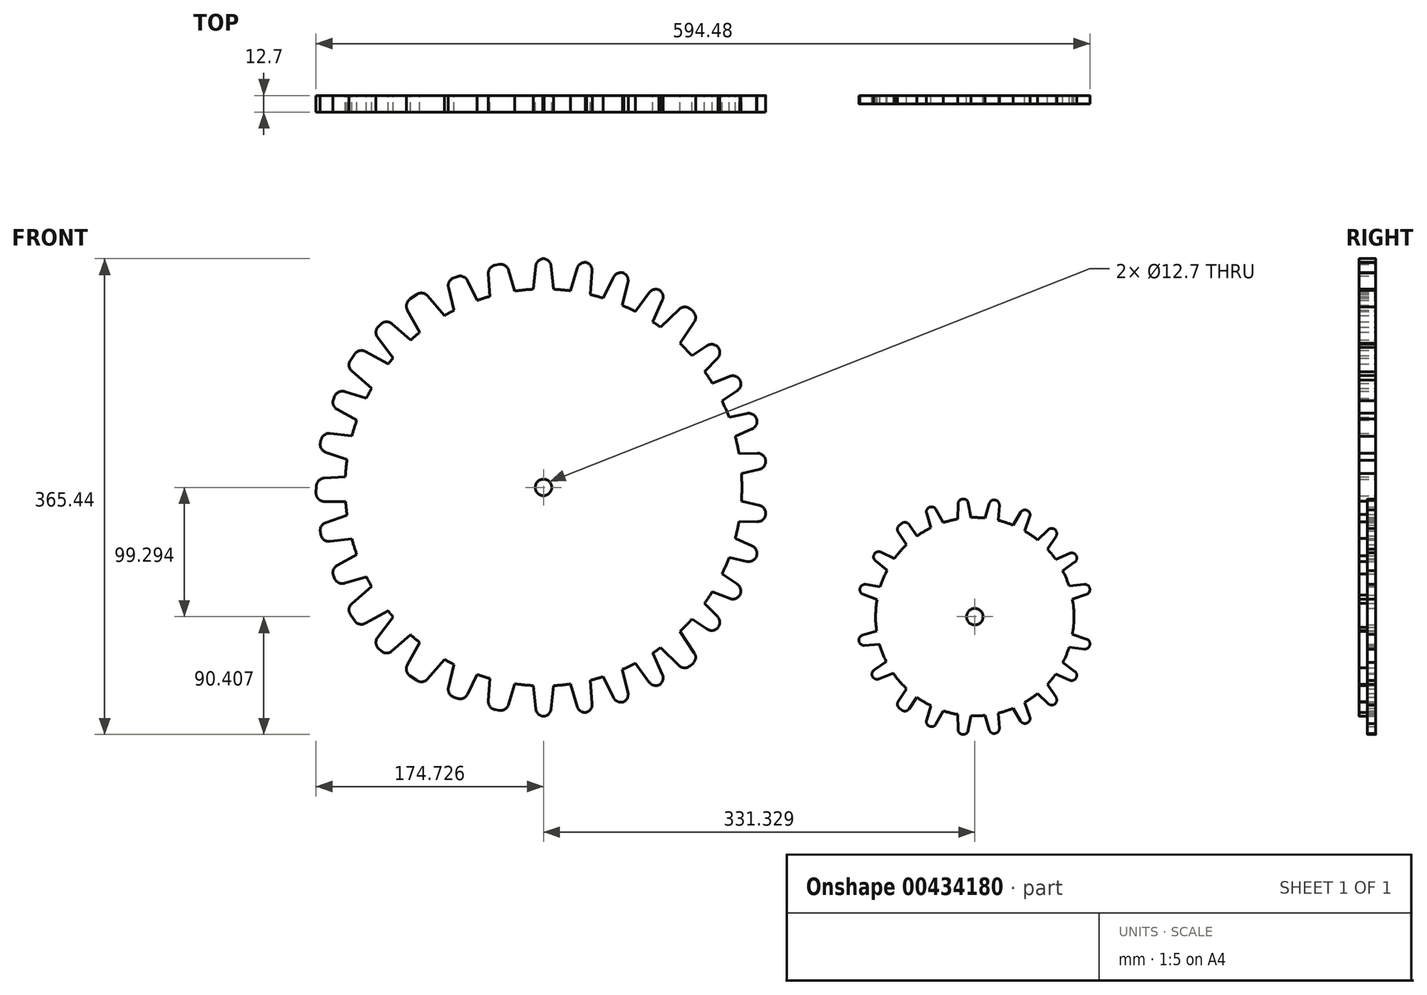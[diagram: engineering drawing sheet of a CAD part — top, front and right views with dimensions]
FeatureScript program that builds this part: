
annotation { "Feature Type Name" : "Feature", "Feature Type Description" : "" }
export const myFeature = defineFeature(function(context is Context, id is Id, definition is map)
    precondition{}
    {
        {
            var Q0;
            Q0=qCreatedBy(makeId("Front.planeOp"),FACE);
            var sketch = newSketch(context, id + "F0", { "sketchPlane" : qUnion([Q0])});
            skCircle(sketch, "E0", {"center": v(-40.91, 6.31) * mm, "radius": 152.4 * mm});
            skCircle(sketch, "E1", {"center": v(290.41, -92.98) * mm, "radius": 76.2 * mm});
            skCircle(sketch, "E2", {"center": v(-40.91, 6.31) * mm, "radius": 6.35 * mm});
            skCircle(sketch, "E3", {"center": v(290.41, -92.98) * mm, "radius": 6.35 * mm});
            skLineSegment(sketch, "E4", {"start": v(214.21, -92.98) * mm, "end": v(366.61, -92.98) * mm, "construction": true});
            skLineSegment(sketch, "E5.bottom", {"start": v(281, -2.62) * mm, "end": v(281.28, -2.6) * mm});
            skLineSegment(sketch, "E5.top", {"start": v(277.33, -17.92) * mm, "end": v(287.54, -16.84) * mm});
            skLineSegment(sketch, "E5.left", {"start": v(277.53, -6.35) * mm, "end": v(277.33, -17.92) * mm});
            skLineSegment(sketch, "E5.right", {"start": v(285.35, -5.65) * mm, "end": v(287.54, -16.84) * mm});
            skPoint(sketch, "E6.visualSharp", {"position": v(277.59, -2.92) * mm});
            skArc(sketch, "E6.filletArc", {"start": v(278, -2.88) * mm, "mid": v(277.7, -3.02) * mm, "end": v(277.58, -3.32) * mm});
            skPoint(sketch, "E7.visualSharp", {"position": v(284.69, -2.3) * mm});
            skArc(sketch, "E7.filletArc", {"start": v(284.77, -2.7) * mm, "mid": v(284.6, -2.42) * mm, "end": v(284.28, -2.33) * mm});
            skLineSegment(sketch, "E8.bottom", {"start": v(305.87, -3.37) * mm, "end": v(306.13, -3.42) * mm});
            skLineSegment(sketch, "E8.top", {"start": v(298.35, -17.2) * mm, "end": v(308.47, -18.95) * mm});
            skLineSegment(sketch, "E8.left", {"start": v(301.54, -6.07) * mm, "end": v(298.35, -17.2) * mm});
            skLineSegment(sketch, "E8.right", {"start": v(309.27, -7.44) * mm, "end": v(308.47, -18.95) * mm});
            skPoint(sketch, "E9.visualSharp", {"position": v(302.49, -2.78) * mm});
            skArc(sketch, "E9.filletArc", {"start": v(302.89, -2.85) * mm, "mid": v(302.57, -2.9) * mm, "end": v(302.38, -3.17) * mm});
            skPoint(sketch, "E10.visualSharp", {"position": v(309.5, -4.01) * mm});
            skArc(sketch, "E10.filletArc", {"start": v(309.48, -4.42) * mm, "mid": v(309.38, -4.11) * mm, "end": v(309.1, -3.94) * mm});
            skLineSegment(sketch, "E11.bottom", {"start": v(330.62, -11.41) * mm, "end": v(330.84, -11.52) * mm});
            skLineSegment(sketch, "E11.top", {"start": v(319.73, -22.65) * mm, "end": v(328.9, -27.21) * mm});
            skLineSegment(sketch, "E11.left", {"start": v(325.62, -12.84) * mm, "end": v(319.73, -22.65) * mm});
            skLineSegment(sketch, "E11.right", {"start": v(332.7, -16.15) * mm, "end": v(328.9, -27.21) * mm});
            skPoint(sketch, "E12.visualSharp", {"position": v(327.45, -9.79) * mm});
            skArc(sketch, "E12.filletArc", {"start": v(327.83, -9.98) * mm, "mid": v(327.5, -9.95) * mm, "end": v(327.23, -10.15) * mm});
            skPoint(sketch, "E13.visualSharp", {"position": v(333.78, -13.03) * mm});
            skArc(sketch, "E13.filletArc", {"start": v(333.65, -13.4) * mm, "mid": v(333.64, -13.08) * mm, "end": v(333.43, -12.85) * mm});
            skLineSegment(sketch, "E14.bottom", {"start": v(255.53, -8.97) * mm, "end": v(255.78, -8.87) * mm});
            skLineSegment(sketch, "E14.top", {"start": v(256.67, -24.66) * mm, "end": v(266.15, -20.75) * mm});
            skLineSegment(sketch, "E14.left", {"start": v(253.35, -13.58) * mm, "end": v(256.67, -24.66) * mm});
            skLineSegment(sketch, "E14.right", {"start": v(260.6, -10.56) * mm, "end": v(266.15, -20.75) * mm});
            skPoint(sketch, "E15.visualSharp", {"position": v(252.37, -10.3) * mm});
            skArc(sketch, "E15.filletArc", {"start": v(252.74, -10.13) * mm, "mid": v(252.5, -10.36) * mm, "end": v(252.48, -10.68) * mm});
            skPoint(sketch, "E16.visualSharp", {"position": v(258.95, -7.55) * mm});
            skArc(sketch, "E16.filletArc", {"start": v(259.14, -7.9) * mm, "mid": v(258.9, -7.7) * mm, "end": v(258.57, -7.7) * mm});
            skLineSegment(sketch, "E17.bottom", {"start": v(232.31, -22.96) * mm, "end": v(234.21, -21.37) * mm});
            skLineSegment(sketch, "E17.top", {"start": v(238.08, -37.6) * mm, "end": v(245.99, -31.07) * mm});
            skLineSegment(sketch, "E17.left", {"start": v(231.6, -28) * mm, "end": v(238.08, -37.6) * mm});
            skLineSegment(sketch, "E17.right", {"start": v(239.8, -22.12) * mm, "end": v(245.99, -31.07) * mm});
            skPoint(sketch, "E18.visualSharp", {"position": v(229.69, -25.16) * mm});
            skArc(sketch, "E18.filletArc", {"start": v(230, -24.9) * mm, "mid": v(229.84, -25.19) * mm, "end": v(229.92, -25.5) * mm});
            skPoint(sketch, "E19.visualSharp", {"position": v(237.42, -18.68) * mm});
            skArc(sketch, "E19.filletArc", {"start": v(237.64, -19.02) * mm, "mid": v(237.34, -18.9) * mm, "end": v(237.03, -19) * mm});
            skLineSegment(sketch, "E20.bottom", {"start": v(213.25, -44.93) * mm, "end": v(213.4, -44.7) * mm});
            skLineSegment(sketch, "E20.top", {"start": v(223.17, -57.14) * mm, "end": v(228.6, -48.42) * mm});
            skLineSegment(sketch, "E20.left", {"start": v(214.1, -49.95) * mm, "end": v(223.17, -57.14) * mm});
            skLineSegment(sketch, "E20.right", {"start": v(218.3, -43.33) * mm, "end": v(228.6, -48.42) * mm});
            skPoint(sketch, "E21.visualSharp", {"position": v(211.41, -47.82) * mm});
            skArc(sketch, "E21.filletArc", {"start": v(211.63, -47.48) * mm, "mid": v(211.57, -47.8) * mm, "end": v(211.73, -48.08) * mm});
            skPoint(sketch, "E22.visualSharp", {"position": v(215.23, -41.8) * mm});
            skArc(sketch, "E22.filletArc", {"start": v(215.6, -41.99) * mm, "mid": v(215.27, -41.96) * mm, "end": v(215.01, -42.15) * mm});
            skLineSegment(sketch, "E23.bottom", {"start": v(202.22, -71.24) * mm, "end": v(202.3, -70.97) * mm});
            skLineSegment(sketch, "E23.top", {"start": v(215.34, -79.93) * mm, "end": v(217.78, -69.95) * mm});
            skLineSegment(sketch, "E23.left", {"start": v(204.54, -75.78) * mm, "end": v(215.34, -79.93) * mm});
            skLineSegment(sketch, "E23.right", {"start": v(206.56, -68.2) * mm, "end": v(217.78, -69.95) * mm});
            skPoint(sketch, "E24.visualSharp", {"position": v(201.34, -74.55) * mm});
            skArc(sketch, "E24.filletArc", {"start": v(201.44, -74.16) * mm, "mid": v(201.48, -74.48) * mm, "end": v(201.72, -74.7) * mm});
            skPoint(sketch, "E25.visualSharp", {"position": v(203.18, -67.67) * mm});
            skArc(sketch, "E25.filletArc", {"start": v(203.58, -67.73) * mm, "mid": v(203.27, -67.8) * mm, "end": v(203.08, -68.06) * mm});
            skLineSegment(sketch, "E26.bottom", {"start": v(352.11, -26.2) * mm, "end": v(352.26, -26.34) * mm});
            skLineSegment(sketch, "E26.top", {"start": v(338.67, -34.01) * mm, "end": v(346.12, -41) * mm});
            skLineSegment(sketch, "E26.left", {"start": v(346.8, -26.17) * mm, "end": v(338.67, -34.01) * mm});
            skLineSegment(sketch, "E26.right", {"start": v(352.74, -31.18) * mm, "end": v(346.12, -41) * mm});
            skPoint(sketch, "E27.visualSharp", {"position": v(349.46, -23.6) * mm});
            skArc(sketch, "E27.filletArc", {"start": v(349.78, -23.9) * mm, "mid": v(349.46, -23.77) * mm, "end": v(349.15, -23.9) * mm});
            skPoint(sketch, "E28.visualSharp", {"position": v(354.51, -28.56) * mm});
            skArc(sketch, "E28.filletArc", {"start": v(354.3, -28.87) * mm, "mid": v(354.38, -28.57) * mm, "end": v(354.25, -28.3) * mm});
            skLineSegment(sketch, "E29.bottom", {"start": v(368.1, -45.7) * mm, "end": v(368.24, -45.94) * mm});
            skLineSegment(sketch, "E29.top", {"start": v(352.64, -49) * mm, "end": v(358, -57.77) * mm});
            skLineSegment(sketch, "E29.left", {"start": v(363.32, -44.24) * mm, "end": v(352.64, -49) * mm});
            skLineSegment(sketch, "E29.right", {"start": v(367.25, -51.04) * mm, "end": v(358, -57.77) * mm});
            skPoint(sketch, "E30.visualSharp", {"position": v(366.34, -42.9) * mm});
            skArc(sketch, "E30.filletArc", {"start": v(366.55, -43.23) * mm, "mid": v(366.3, -43.04) * mm, "end": v(365.98, -43.06) * mm});
            skPoint(sketch, "E31.visualSharp", {"position": v(370.13, -48.95) * mm});
            skArc(sketch, "E31.filletArc", {"start": v(369.79, -49.2) * mm, "mid": v(369.96, -48.92) * mm, "end": v(369.9, -48.6) * mm});
            skLineSegment(sketch, "E32.bottom", {"start": v(378.65, -70.95) * mm, "end": v(378.72, -71.22) * mm});
            skLineSegment(sketch, "E32.top", {"start": v(362.91, -69.52) * mm, "end": v(365.4, -79.49) * mm});
            skLineSegment(sketch, "E32.left", {"start": v(374.5, -68.13) * mm, "end": v(362.91, -69.52) * mm});
            skLineSegment(sketch, "E32.right", {"start": v(376.26, -75.79) * mm, "end": v(365.4, -79.49) * mm});
            skPoint(sketch, "E33.visualSharp", {"position": v(377.8, -67.74) * mm});
            skArc(sketch, "E33.filletArc", {"start": v(377.9, -68.12) * mm, "mid": v(377.72, -67.86) * mm, "end": v(377.41, -67.78) * mm});
            skPoint(sketch, "E34.visualSharp", {"position": v(379.6, -74.65) * mm});
            skArc(sketch, "E34.filletArc", {"start": v(379.21, -74.78) * mm, "mid": v(379.46, -74.57) * mm, "end": v(379.5, -74.24) * mm});
            skArc(sketch, "E35.MirrorCS", {"start": v(259.14, -178.06) * mm, "mid": v(258.9, -178.27) * mm, "end": v(258.57, -178.26) * mm});
            skArc(sketch, "E36.MirrorCS", {"start": v(278, -183.08) * mm, "mid": v(277.7, -182.94) * mm, "end": v(277.58, -182.64) * mm});
            skArc(sketch, "E37.MirrorCS", {"start": v(366.55, -142.74) * mm, "mid": v(366.3, -142.93) * mm, "end": v(365.98, -142.91) * mm});
            skArc(sketch, "E38.MirrorCS", {"start": v(309.48, -181.54) * mm, "mid": v(309.38, -181.85) * mm, "end": v(309.1, -182.02) * mm});
            skLineSegment(sketch, "E39.MirrorCS", {"start": v(352.11, -159.77) * mm, "end": v(352.26, -159.63) * mm});
            skArc(sketch, "E40.MirrorCS", {"start": v(349.78, -162.06) * mm, "mid": v(349.46, -162.2) * mm, "end": v(349.15, -162.07) * mm});
            skArc(sketch, "E41.MirrorCS", {"start": v(377.9, -117.85) * mm, "mid": v(377.72, -118.1) * mm, "end": v(377.41, -118.18) * mm});
            skArc(sketch, "E42.MirrorCS", {"start": v(327.83, -175.99) * mm, "mid": v(327.5, -176.02) * mm, "end": v(327.23, -175.82) * mm});
            skArc(sketch, "E43.MirrorCS", {"start": v(354.3, -157.1) * mm, "mid": v(354.38, -157.4) * mm, "end": v(354.25, -157.67) * mm});
            skLineSegment(sketch, "E44.MirrorCS", {"start": v(368.1, -140.26) * mm, "end": v(368.24, -140.03) * mm});
            skLineSegment(sketch, "E45.MirrorCS", {"start": v(281, -183.35) * mm, "end": v(281.28, -183.37) * mm});
            skArc(sketch, "E46.MirrorCS", {"start": v(252.74, -175.83) * mm, "mid": v(252.5, -175.6) * mm, "end": v(252.48, -175.28) * mm});
            skArc(sketch, "E47.MirrorCS", {"start": v(284.77, -183.27) * mm, "mid": v(284.6, -183.55) * mm, "end": v(284.28, -183.64) * mm});
            skLineSegment(sketch, "E48.MirrorCS", {"start": v(330.62, -174.56) * mm, "end": v(330.84, -174.44) * mm});
            skArc(sketch, "E49.MirrorCS", {"start": v(237.64, -166.94) * mm, "mid": v(237.34, -167.07) * mm, "end": v(237.03, -166.97) * mm});
            skArc(sketch, "E50.MirrorCS", {"start": v(369.79, -136.76) * mm, "mid": v(369.96, -137.04) * mm, "end": v(369.9, -137.37) * mm});
            skLineSegment(sketch, "E51.MirrorCS", {"start": v(255.53, -177) * mm, "end": v(255.78, -177.1) * mm});
            skArc(sketch, "E52.MirrorCS", {"start": v(333.65, -172.57) * mm, "mid": v(333.64, -172.88) * mm, "end": v(333.43, -173.12) * mm});
            skLineSegment(sketch, "E53.MirrorCS", {"start": v(232.31, -163) * mm, "end": v(234.21, -164.6) * mm});
            skArc(sketch, "E54.MirrorCS", {"start": v(230, -161.06) * mm, "mid": v(229.84, -160.78) * mm, "end": v(229.92, -160.46) * mm});
            skLineSegment(sketch, "E55.MirrorCS", {"start": v(305.87, -182.6) * mm, "end": v(306.13, -182.55) * mm});
            skArc(sketch, "E56.MirrorCS", {"start": v(302.89, -183.12) * mm, "mid": v(302.57, -183.06) * mm, "end": v(302.38, -182.8) * mm});
            skLineSegment(sketch, "E57.MirrorCS", {"start": v(378.65, -115.01) * mm, "end": v(378.72, -114.74) * mm});
            skArc(sketch, "E58.MirrorCS", {"start": v(379.21, -111.18) * mm, "mid": v(379.46, -111.4) * mm, "end": v(379.5, -111.73) * mm});
            skPoint(sketch, "E59.MirrorP", {"position": v(354.51, -157.4) * mm});
            skPoint(sketch, "E60.MirrorP", {"position": v(258.95, -178.42) * mm});
            skLineSegment(sketch, "E61.MirrorCS", {"start": v(285.35, -180.31) * mm, "end": v(287.54, -169.13) * mm});
            skPoint(sketch, "E62.MirrorP", {"position": v(277.59, -183.05) * mm});
            skPoint(sketch, "E63.MirrorP", {"position": v(379.6, -111.32) * mm});
            skPoint(sketch, "E64.MirrorP", {"position": v(237.42, -167.29) * mm});
            skLineSegment(sketch, "E65.MirrorCS", {"start": v(332.7, -169.81) * mm, "end": v(328.9, -158.75) * mm});
            skLineSegment(sketch, "E66.MirrorCS", {"start": v(231.6, -157.96) * mm, "end": v(238.08, -148.36) * mm});
            skPoint(sketch, "E67.MirrorP", {"position": v(229.69, -160.8) * mm});
            skLineSegment(sketch, "E68.MirrorCS", {"start": v(256.67, -161.3) * mm, "end": v(266.15, -165.22) * mm});
            skLineSegment(sketch, "E69.MirrorCS", {"start": v(260.6, -175.4) * mm, "end": v(266.15, -165.22) * mm});
            skLineSegment(sketch, "E70.MirrorCS", {"start": v(325.62, -173.13) * mm, "end": v(319.73, -163.32) * mm});
            skLineSegment(sketch, "E71.MirrorCS", {"start": v(374.5, -117.83) * mm, "end": v(362.91, -116.45) * mm});
            skPoint(sketch, "E72.MirrorP", {"position": v(327.45, -176.18) * mm});
            skLineSegment(sketch, "E73.MirrorCS", {"start": v(298.35, -168.77) * mm, "end": v(308.47, -167.01) * mm});
            skLineSegment(sketch, "E74.MirrorCS", {"start": v(362.91, -116.45) * mm, "end": v(365.4, -106.48) * mm});
            skPoint(sketch, "E75.MirrorP", {"position": v(366.34, -143.07) * mm});
            skPoint(sketch, "E76.MirrorP", {"position": v(370.13, -137.01) * mm});
            skLineSegment(sketch, "E77.MirrorCS", {"start": v(367.25, -134.92) * mm, "end": v(358, -128.2) * mm});
            skPoint(sketch, "E78.MirrorP", {"position": v(349.46, -162.37) * mm});
            skPoint(sketch, "E79.MirrorP", {"position": v(252.37, -175.67) * mm});
            skPoint(sketch, "E80.MirrorP", {"position": v(284.69, -183.67) * mm});
            skLineSegment(sketch, "E81.MirrorCS", {"start": v(301.54, -179.9) * mm, "end": v(298.35, -168.77) * mm});
            skLineSegment(sketch, "E82.MirrorCS", {"start": v(352.74, -154.78) * mm, "end": v(346.12, -144.97) * mm});
            skLineSegment(sketch, "E83.MirrorCS", {"start": v(376.26, -110.18) * mm, "end": v(365.4, -106.48) * mm});
            skLineSegment(sketch, "E84.MirrorCS", {"start": v(238.08, -148.36) * mm, "end": v(245.99, -154.9) * mm});
            skLineSegment(sketch, "E85.MirrorCS", {"start": v(346.8, -159.8) * mm, "end": v(338.67, -151.95) * mm});
            skLineSegment(sketch, "E86.MirrorCS", {"start": v(309.27, -178.53) * mm, "end": v(308.47, -167.01) * mm});
            skPoint(sketch, "E87.MirrorP", {"position": v(309.5, -181.95) * mm});
            skLineSegment(sketch, "E88.MirrorCS", {"start": v(319.73, -163.32) * mm, "end": v(328.9, -158.75) * mm});
            skLineSegment(sketch, "E89.MirrorCS", {"start": v(253.35, -172.39) * mm, "end": v(256.67, -161.3) * mm});
            skLineSegment(sketch, "E90.MirrorCS", {"start": v(277.53, -179.62) * mm, "end": v(277.33, -168.05) * mm});
            skPoint(sketch, "E91.MirrorP", {"position": v(333.78, -172.94) * mm});
            skLineSegment(sketch, "E92.MirrorCS", {"start": v(338.67, -151.95) * mm, "end": v(346.12, -144.97) * mm});
            skPoint(sketch, "E93.MirrorP", {"position": v(302.49, -183.19) * mm});
            skPoint(sketch, "E94.MirrorP", {"position": v(377.8, -118.23) * mm});
            skLineSegment(sketch, "E95.MirrorCS", {"start": v(239.8, -163.85) * mm, "end": v(245.99, -154.9) * mm});
            skLineSegment(sketch, "E96.MirrorCS", {"start": v(363.32, -141.72) * mm, "end": v(352.64, -136.97) * mm});
            skLineSegment(sketch, "E97.MirrorCS", {"start": v(277.33, -168.05) * mm, "end": v(287.54, -169.13) * mm});
            skLineSegment(sketch, "E98.MirrorCS", {"start": v(352.64, -136.97) * mm, "end": v(358, -128.2) * mm});
            skLineSegment(sketch, "E99", {"start": v(-193.31, 6.31) * mm, "end": v(111.49, 6.31) * mm, "construction": true});
            skLineSegment(sketch, "E100.bottom", {"start": v(-215.94, -4) * mm, "end": v(-215.1, 12.77) * mm});
            skLineSegment(sketch, "E100.top", {"start": v(-192.93, -4.45) * mm, "end": v(-193.1, 14.48) * mm});
            skLineSegment(sketch, "E100.left", {"start": v(-209.28, -4.48) * mm, "end": v(-192.93, -4.45) * mm});
            skLineSegment(sketch, "E100.right", {"start": v(-209.4, 13.51) * mm, "end": v(-193.1, 14.48) * mm});
            skPoint(sketch, "E101.visualSharp", {"position": v(-215.96, -4.49) * mm});
            skArc(sketch, "E101.filletArc", {"start": v(-215.94, -4) * mm, "mid": v(-215.81, -4.35) * mm, "end": v(-215.48, -4.49) * mm});
            skPoint(sketch, "E102.visualSharp", {"position": v(-215.09, 13.18) * mm});
            skArc(sketch, "E102.filletArc", {"start": v(-214.68, 13.2) * mm, "mid": v(-214.98, 13.07) * mm, "end": v(-215.1, 12.77) * mm});
            skLineSegment(sketch, "E103.bottom", {"start": v(-212.29, 40.71) * mm, "end": v(-211.8, 42.9) * mm});
            skLineSegment(sketch, "E103.top", {"start": v(-191.8, 27.73) * mm, "end": v(-188.1, 45.82) * mm});
            skLineSegment(sketch, "E103.left", {"start": v(-208.14, 33.3) * mm, "end": v(-191.8, 27.73) * mm});
            skLineSegment(sketch, "E103.right", {"start": v(-204.86, 47.8) * mm, "end": v(-188.1, 45.82) * mm});
            skPoint(sketch, "E104.visualSharp", {"position": v(-213.55, 35.14) * mm});
            skArc(sketch, "E104.filletArc", {"start": v(-213.46, 35.53) * mm, "mid": v(-213.42, 35.21) * mm, "end": v(-213.17, 35) * mm});
            skPoint(sketch, "E105.visualSharp", {"position": v(-210.53, 48.46) * mm});
            skArc(sketch, "E105.filletArc", {"start": v(-210.12, 48.41) * mm, "mid": v(-210.44, 48.33) * mm, "end": v(-210.62, 48.06) * mm});
            skLineSegment(sketch, "E106.bottom", {"start": v(-202.2, 74.2) * mm, "end": v(-201.34, 76.26) * mm});
            skLineSegment(sketch, "E106.top", {"start": v(-184.28, 58) * mm, "end": v(-177, 74.91) * mm});
            skLineSegment(sketch, "E106.left", {"start": v(-199.36, 66.2) * mm, "end": v(-184.28, 58) * mm});
            skLineSegment(sketch, "E106.right", {"start": v(-193.65, 79.9) * mm, "end": v(-177, 74.91) * mm});
            skPoint(sketch, "E107.visualSharp", {"position": v(-204.38, 68.92) * mm});
            skArc(sketch, "E107.filletArc", {"start": v(-204.23, 69.3) * mm, "mid": v(-204.23, 68.98) * mm, "end": v(-204.02, 68.73) * mm});
            skPoint(sketch, "E108.visualSharp", {"position": v(-199.14, 81.56) * mm});
            skArc(sketch, "E108.filletArc", {"start": v(-198.75, 81.44) * mm, "mid": v(-199.08, 81.41) * mm, "end": v(-199.3, 81.18) * mm});
            skLineSegment(sketch, "E109.bottom", {"start": v(-189.2, 104.13) * mm, "end": v(-185.93, 108.8) * mm});
            skLineSegment(sketch, "E109.top", {"start": v(-172.93, 82.46) * mm, "end": v(-160.25, 101.1) * mm});
            skLineSegment(sketch, "E109.left", {"start": v(-188.16, 95.7) * mm, "end": v(-172.93, 82.46) * mm});
            skLineSegment(sketch, "E109.right", {"start": v(-177.66, 110.71) * mm, "end": v(-160.25, 101.1) * mm});
            skPoint(sketch, "E110.visualSharp", {"position": v(-192.47, 99.45) * mm});
            skArc(sketch, "E110.filletArc", {"start": v(-191.53, 99.22) * mm, "mid": v(-192.18, 99.85) * mm, "end": v(-191.58, 99.18) * mm});
            skPoint(sketch, "E111.visualSharp", {"position": v(-182.65, 113.47) * mm});
            skArc(sketch, "E111.filletArc", {"start": v(-182.09, 112.72) * mm, "mid": v(-182.93, 113.06) * mm, "end": v(-182.11, 112.67) * mm});
            skLineSegment(sketch, "E112.bottom", {"start": v(-167.6, 130.11) * mm, "end": v(-165.73, 131.84) * mm});
            skLineSegment(sketch, "E112.top", {"start": v(-156.49, 105.65) * mm, "end": v(-142.97, 119.5) * mm});
            skLineSegment(sketch, "E112.left", {"start": v(-168.4, 121.65) * mm, "end": v(-156.49, 105.65) * mm});
            skLineSegment(sketch, "E112.right", {"start": v(-157.25, 131.96) * mm, "end": v(-142.97, 119.5) * mm});
            skPoint(sketch, "E113.visualSharp", {"position": v(-171.8, 126.24) * mm});
            skArc(sketch, "E113.filletArc", {"start": v(-170.94, 125.81) * mm, "mid": v(-171.43, 126.57) * mm, "end": v(-171, 125.78) * mm});
            skPoint(sketch, "E114.visualSharp", {"position": v(-161.54, 135.7) * mm});
            skArc(sketch, "E114.filletArc", {"start": v(-161.14, 134.86) * mm, "mid": v(-161.9, 135.36) * mm, "end": v(-161.18, 134.8) * mm});
            skLineSegment(sketch, "E115.bottom", {"start": v(-143.55, 150.83) * mm, "end": v(-138.34, 154.48) * mm});
            skLineSegment(sketch, "E115.top", {"start": v(-135.97, 125.43) * mm, "end": v(-116.9, 138.42) * mm});
            skLineSegment(sketch, "E115.left", {"start": v(-145.46, 142.55) * mm, "end": v(-135.97, 125.43) * mm});
            skLineSegment(sketch, "E115.right", {"start": v(-129.9, 153.43) * mm, "end": v(-116.9, 138.42) * mm});
            skPoint(sketch, "E116.visualSharp", {"position": v(-148.23, 147.55) * mm});
            skArc(sketch, "E116.filletArc", {"start": v(-147.43, 147.01) * mm, "mid": v(-147.81, 147.83) * mm, "end": v(-147.5, 146.98) * mm});
            skPoint(sketch, "E117.visualSharp", {"position": v(-133.65, 157.76) * mm});
            skArc(sketch, "E117.filletArc", {"start": v(-133.37, 156.88) * mm, "mid": v(-134.05, 157.47) * mm, "end": v(-133.42, 156.82) * mm});
            skLineSegment(sketch, "E118.bottom", {"start": v(-109.94, 167.25) * mm, "end": v(-107.13, 168.27) * mm});
            skLineSegment(sketch, "E118.top", {"start": v(-109.6, 142.36) * mm, "end": v(-91.8, 149.96) * mm});
            skLineSegment(sketch, "E118.left", {"start": v(-113.93, 159.74) * mm, "end": v(-109.6, 142.36) * mm});
            skLineSegment(sketch, "E118.right", {"start": v(-99.27, 165.1) * mm, "end": v(-91.8, 149.96) * mm});
            skPoint(sketch, "E119.visualSharp", {"position": v(-115.31, 165.3) * mm});
            skArc(sketch, "E119.filletArc", {"start": v(-114.67, 164.56) * mm, "mid": v(-114.85, 165.45) * mm, "end": v(-114.73, 164.55) * mm});
            skPoint(sketch, "E120.visualSharp", {"position": v(-101.78, 170.22) * mm});
            skArc(sketch, "E120.filletArc", {"start": v(-101.75, 169.28) * mm, "mid": v(-102.24, 170.04) * mm, "end": v(-101.8, 169.25) * mm});
            skLineSegment(sketch, "E121.bottom", {"start": v(-78.06, 177.02) * mm, "end": v(-74.96, 177.57) * mm});
            skLineSegment(sketch, "E121.top", {"start": v(-82.09, 153.04) * mm, "end": v(-63.13, 157.08) * mm});
            skLineSegment(sketch, "E121.left", {"start": v(-83.3, 170.32) * mm, "end": v(-82.09, 153.04) * mm});
            skLineSegment(sketch, "E121.right", {"start": v(-67.76, 173.08) * mm, "end": v(-63.13, 157.08) * mm});
            skPoint(sketch, "E122.visualSharp", {"position": v(-83.7, 176.03) * mm});
            skArc(sketch, "E122.filletArc", {"start": v(-83.3, 176.1) * mm, "mid": v(-83.57, 175.93) * mm, "end": v(-83.66, 175.62) * mm});
            skPoint(sketch, "E123.visualSharp", {"position": v(-69.34, 178.56) * mm});
            skArc(sketch, "E123.filletArc", {"start": v(-69.23, 178.17) * mm, "mid": v(-69.43, 178.42) * mm, "end": v(-69.74, 178.49) * mm});
            skLineSegment(sketch, "E124.bottom", {"start": v(-41.36, 182.05) * mm, "end": v(-40.47, 182.05) * mm});
            skLineSegment(sketch, "E124.top", {"start": v(-48.66, 158.51) * mm, "end": v(-33.16, 158.51) * mm});
            skLineSegment(sketch, "E124.left", {"start": v(-46.79, 176.36) * mm, "end": v(-48.66, 158.51) * mm});
            skLineSegment(sketch, "E124.right", {"start": v(-35.04, 176.36) * mm, "end": v(-33.16, 158.51) * mm});
            skPoint(sketch, "E125.visualSharp", {"position": v(-46.19, 182.05) * mm});
            skArc(sketch, "E125.filletArc", {"start": v(-45.78, 182.05) * mm, "mid": v(-46.09, 181.93) * mm, "end": v(-46.23, 181.64) * mm});
            skPoint(sketch, "E126.visualSharp", {"position": v(-35.64, 182.05) * mm});
            skArc(sketch, "E126.filletArc", {"start": v(-35.6, 181.64) * mm, "mid": v(-35.74, 181.93) * mm, "end": v(-36.05, 182.05) * mm});
            skLineSegment(sketch, "E127.bottom", {"start": v(-8.75, 179.18) * mm, "end": v(-7.88, 179.03) * mm});
            skLineSegment(sketch, "E127.top", {"start": v(-20.03, 157.27) * mm, "end": v(-4.82, 154.38) * mm});
            skLineSegment(sketch, "E127.left", {"start": v(-15.09, 174.53) * mm, "end": v(-20.03, 157.27) * mm});
            skLineSegment(sketch, "E127.right", {"start": v(-3.52, 172.48) * mm, "end": v(-4.82, 154.38) * mm});
            skPoint(sketch, "E128.visualSharp", {"position": v(-13.51, 180.02) * mm});
            skArc(sketch, "E128.filletArc", {"start": v(-13.1, 179.95) * mm, "mid": v(-13.43, 179.9) * mm, "end": v(-13.62, 179.63) * mm});
            skPoint(sketch, "E129.visualSharp", {"position": v(-3.11, 178.19) * mm});
            skArc(sketch, "E129.filletArc", {"start": v(-3.14, 177.78) * mm, "mid": v(-3.24, 178.1) * mm, "end": v(-3.51, 178.26) * mm});
            skLineSegment(sketch, "E130.bottom", {"start": v(19.96, 171.23) * mm, "end": v(20.8, 170.93) * mm});
            skLineSegment(sketch, "E130.top", {"start": v(5.05, 151.62) * mm, "end": v(19.56, 146.2) * mm});
            skLineSegment(sketch, "E130.left", {"start": v(12.92, 167.75) * mm, "end": v(5.05, 151.62) * mm});
            skLineSegment(sketch, "E130.right", {"start": v(23.95, 163.72) * mm, "end": v(19.56, 146.2) * mm});
            skPoint(sketch, "E131.visualSharp", {"position": v(15.42, 172.89) * mm});
            skArc(sketch, "E131.filletArc", {"start": v(15.8, 172.75) * mm, "mid": v(15.48, 172.74) * mm, "end": v(15.24, 172.52) * mm});
            skPoint(sketch, "E132.visualSharp", {"position": v(25.34, 169.28) * mm});
            skArc(sketch, "E132.filletArc", {"start": v(25.24, 168.88) * mm, "mid": v(25.2, 169.2) * mm, "end": v(24.96, 169.42) * mm});
            skLineSegment(sketch, "E133.bottom", {"start": v(47.82, 158.08) * mm, "end": v(48.58, 157.64) * mm});
            skLineSegment(sketch, "E133.top", {"start": v(29.72, 141.35) * mm, "end": v(43.07, 133.48) * mm});
            skLineSegment(sketch, "E133.left", {"start": v(40.27, 155.87) * mm, "end": v(29.72, 141.35) * mm});
            skLineSegment(sketch, "E133.right", {"start": v(50.44, 150) * mm, "end": v(43.07, 133.48) * mm});
            skPoint(sketch, "E134.visualSharp", {"position": v(43.63, 160.5) * mm});
            skArc(sketch, "E134.filletArc", {"start": v(43.99, 160.3) * mm, "mid": v(43.67, 160.35) * mm, "end": v(43.4, 160.17) * mm});
            skPoint(sketch, "E135.visualSharp", {"position": v(52.77, 155.22) * mm});
            skArc(sketch, "E135.filletArc", {"start": v(52.6, 154.85) * mm, "mid": v(52.63, 155.17) * mm, "end": v(52.42, 155.43) * mm});
            skLineSegment(sketch, "E136.bottom", {"start": v(71.75, 143.36) * mm, "end": v(73.75, 141.63) * mm});
            skLineSegment(sketch, "E136.top", {"start": v(48.98, 129.38) * mm, "end": v(63.88, 116.97) * mm});
            skLineSegment(sketch, "E136.left", {"start": v(63.2, 143.11) * mm, "end": v(48.98, 129.38) * mm});
            skLineSegment(sketch, "E136.right", {"start": v(74.87, 133.27) * mm, "end": v(63.88, 116.97) * mm});
            skPoint(sketch, "E137.visualSharp", {"position": v(67.36, 147.13) * mm});
            skArc(sketch, "E137.filletArc", {"start": v(67.05, 146.2) * mm, "mid": v(67.72, 146.82) * mm, "end": v(67.03, 146.23) * mm});
            skPoint(sketch, "E138.visualSharp", {"position": v(78.03, 137.95) * mm});
            skArc(sketch, "E138.filletArc", {"start": v(77.2, 137.47) * mm, "mid": v(77.66, 138.26) * mm, "end": v(77.18, 137.5) * mm});
            skLineSegment(sketch, "E139.bottom", {"start": v(93.2, 113.89) * mm, "end": v(93.27, 113.8) * mm});
            skLineSegment(sketch, "E139.top", {"start": v(73.17, 107.35) * mm, "end": v(82.83, 95.26) * mm});
            skLineSegment(sketch, "E139.left", {"start": v(84.72, 115.14) * mm, "end": v(73.17, 107.35) * mm});
            skLineSegment(sketch, "E139.right", {"start": v(92.77, 105.56) * mm, "end": v(82.83, 95.26) * mm});
            skPoint(sketch, "E140.visualSharp", {"position": v(89.62, 118.45) * mm});
            skArc(sketch, "E140.filletArc", {"start": v(89.88, 118.12) * mm, "mid": v(89.6, 118.28) * mm, "end": v(89.27, 118.21) * mm});
            skPoint(sketch, "E141.visualSharp", {"position": v(96.62, 109.53) * mm});
            skArc(sketch, "E141.filletArc", {"start": v(96.34, 109.25) * mm, "mid": v(96.47, 109.54) * mm, "end": v(96.37, 109.84) * mm});
            skLineSegment(sketch, "E142.bottom", {"start": v(109.88, 88.9) * mm, "end": v(109.92, 88.83) * mm});
            skLineSegment(sketch, "E142.top", {"start": v(88.8, 86.32) * mm, "end": v(96.25, 72.73) * mm});
            skLineSegment(sketch, "E142.left", {"start": v(102, 91.64) * mm, "end": v(88.8, 86.32) * mm});
            skLineSegment(sketch, "E142.right", {"start": v(107.88, 80.55) * mm, "end": v(96.25, 72.73) * mm});
            skPoint(sketch, "E143.visualSharp", {"position": v(107.2, 93.73) * mm});
            skArc(sketch, "E143.filletArc", {"start": v(107.4, 93.38) * mm, "mid": v(107.15, 93.6) * mm, "end": v(106.83, 93.58) * mm});
            skPoint(sketch, "E144.visualSharp", {"position": v(112.71, 83.8) * mm});
            skArc(sketch, "E144.filletArc", {"start": v(112.37, 83.57) * mm, "mid": v(112.56, 83.84) * mm, "end": v(112.51, 84.17) * mm});
            skLineSegment(sketch, "E145.bottom", {"start": v(122.78, 58.9) * mm, "end": v(122.8, 58.82) * mm});
            skLineSegment(sketch, "E145.top", {"start": v(101.64, 60.21) * mm, "end": v(106.37, 45.45) * mm});
            skLineSegment(sketch, "E145.left", {"start": v(115.46, 63.1) * mm, "end": v(101.64, 60.21) * mm});
            skLineSegment(sketch, "E145.right", {"start": v(119.3, 51.15) * mm, "end": v(106.37, 45.45) * mm});
            skPoint(sketch, "E146.visualSharp", {"position": v(121.06, 64.27) * mm});
            skArc(sketch, "E146.filletArc", {"start": v(121.18, 63.88) * mm, "mid": v(120.98, 64.13) * mm, "end": v(120.66, 64.18) * mm});
            skPoint(sketch, "E147.visualSharp", {"position": v(124.53, 53.46) * mm});
            skArc(sketch, "E147.filletArc", {"start": v(124.15, 53.3) * mm, "mid": v(124.38, 53.52) * mm, "end": v(124.4, 53.85) * mm});
            skLineSegment(sketch, "E148.bottom", {"start": v(129.76, 27.12) * mm, "end": v(129.77, 27.03) * mm});
            skLineSegment(sketch, "E148.top", {"start": v(109.24, 32.35) * mm, "end": v(111.11, 16.97) * mm});
            skLineSegment(sketch, "E148.left", {"start": v(123.34, 32.62) * mm, "end": v(109.24, 32.35) * mm});
            skLineSegment(sketch, "E148.right", {"start": v(124.9, 20.17) * mm, "end": v(111.11, 16.97) * mm});
            skPoint(sketch, "E149.visualSharp", {"position": v(129.08, 32.73) * mm});
            skArc(sketch, "E149.filletArc", {"start": v(129.13, 32.33) * mm, "mid": v(128.98, 32.61) * mm, "end": v(128.67, 32.72) * mm});
            skPoint(sketch, "E150.visualSharp", {"position": v(130.44, 21.46) * mm});
            skArc(sketch, "E150.filletArc", {"start": v(130.04, 21.37) * mm, "mid": v(130.3, 21.55) * mm, "end": v(130.39, 21.87) * mm});
            skArc(sketch, "E151.MirrorCS", {"start": v(25.24, -156.26) * mm, "mid": v(25.2, -156.58) * mm, "end": v(24.96, -156.8) * mm});
            skArc(sketch, "E152.MirrorCS", {"start": v(-3.14, -165.16) * mm, "mid": v(-3.24, -165.47) * mm, "end": v(-3.51, -165.64) * mm});
            skArc(sketch, "E153.MirrorCS", {"start": v(-170.94, -113.19) * mm, "mid": v(-171.43, -113.95) * mm, "end": v(-171, -113.15) * mm});
            skArc(sketch, "E154.MirrorCS", {"start": v(130.04, -8.75) * mm, "mid": v(130.3, -8.93) * mm, "end": v(130.39, -9.24) * mm});
            skArc(sketch, "E155.MirrorCS", {"start": v(-35.6, -169.02) * mm, "mid": v(-35.74, -169.31) * mm, "end": v(-36.05, -169.43) * mm});
            skArc(sketch, "E156.MirrorCS", {"start": v(77.2, -124.85) * mm, "mid": v(77.66, -125.63) * mm, "end": v(77.18, -124.87) * mm});
            skLineSegment(sketch, "E157.MirrorCS", {"start": v(19.96, -158.61) * mm, "end": v(20.8, -158.3) * mm});
            skLineSegment(sketch, "E158.MirrorCS", {"start": v(-109.94, -154.62) * mm, "end": v(-107.13, -155.64) * mm});
            skArc(sketch, "E159.MirrorCS", {"start": v(52.6, -142.22) * mm, "mid": v(52.63, -142.55) * mm, "end": v(52.42, -142.8) * mm});
            skArc(sketch, "E160.MirrorCS", {"start": v(-45.78, -169.43) * mm, "mid": v(-46.09, -169.31) * mm, "end": v(-46.23, -169.02) * mm});
            skLineSegment(sketch, "E161.MirrorCS", {"start": v(71.75, -130.73) * mm, "end": v(73.75, -129) * mm});
            skLineSegment(sketch, "E162.MirrorCS", {"start": v(109.88, -76.28) * mm, "end": v(109.92, -76.2) * mm});
            skArc(sketch, "E163.MirrorCS", {"start": v(-161.14, -122.24) * mm, "mid": v(-161.9, -122.73) * mm, "end": v(-161.18, -122.18) * mm});
            skArc(sketch, "E164.MirrorCS", {"start": v(-101.75, -156.65) * mm, "mid": v(-102.24, -157.42) * mm, "end": v(-101.8, -156.62) * mm});
            skArc(sketch, "E165.MirrorCS", {"start": v(112.37, -70.95) * mm, "mid": v(112.56, -71.22) * mm, "end": v(112.51, -71.54) * mm});
            skArc(sketch, "E166.MirrorCS", {"start": v(129.13, -19.7) * mm, "mid": v(128.98, -20) * mm, "end": v(128.67, -20.1) * mm});
            skArc(sketch, "E167.MirrorCS", {"start": v(107.4, -80.76) * mm, "mid": v(107.15, -80.97) * mm, "end": v(106.83, -80.96) * mm});
            skArc(sketch, "E168.MirrorCS", {"start": v(-114.67, -151.94) * mm, "mid": v(-114.85, -152.83) * mm, "end": v(-114.73, -151.93) * mm});
            skArc(sketch, "E169.MirrorCS", {"start": v(-182.09, -100.1) * mm, "mid": v(-182.93, -100.44) * mm, "end": v(-182.11, -100.05) * mm});
            skArc(sketch, "E170.MirrorCS", {"start": v(89.88, -105.5) * mm, "mid": v(89.6, -105.66) * mm, "end": v(89.27, -105.59) * mm});
            skArc(sketch, "E171.MirrorCS", {"start": v(121.18, -51.26) * mm, "mid": v(120.98, -51.5) * mm, "end": v(120.66, -51.56) * mm});
            skArc(sketch, "E172.MirrorCS", {"start": v(67.05, -133.58) * mm, "mid": v(67.72, -134.2) * mm, "end": v(67.03, -133.6) * mm});
            skLineSegment(sketch, "E173.MirrorCS", {"start": v(-212.29, -28.09) * mm, "end": v(-211.8, -30.27) * mm});
            skLineSegment(sketch, "E174.MirrorCS", {"start": v(-41.36, -169.43) * mm, "end": v(-40.47, -169.43) * mm});
            skLineSegment(sketch, "E175.MirrorCS", {"start": v(129.76, -14.5) * mm, "end": v(129.77, -14.4) * mm});
            skArc(sketch, "E176.MirrorCS", {"start": v(-69.23, -165.54) * mm, "mid": v(-69.43, -165.8) * mm, "end": v(-69.74, -165.86) * mm});
            skArc(sketch, "E177.MirrorCS", {"start": v(-204.23, -56.68) * mm, "mid": v(-204.23, -56.35) * mm, "end": v(-204.02, -56.1) * mm});
            skLineSegment(sketch, "E178.MirrorCS", {"start": v(-167.6, -117.5) * mm, "end": v(-165.73, -119.22) * mm});
            skArc(sketch, "E179.MirrorCS", {"start": v(-13.1, -167.33) * mm, "mid": v(-13.43, -167.27) * mm, "end": v(-13.62, -167) * mm});
            skArc(sketch, "E180.MirrorCS", {"start": v(-213.46, -22.91) * mm, "mid": v(-213.42, -22.59) * mm, "end": v(-213.17, -22.38) * mm});
            skArc(sketch, "E181.MirrorCS", {"start": v(15.8, -160.12) * mm, "mid": v(15.48, -160.12) * mm, "end": v(15.24, -159.9) * mm});
            skArc(sketch, "E182.MirrorCS", {"start": v(-147.43, -134.39) * mm, "mid": v(-147.81, -135.2) * mm, "end": v(-147.5, -134.36) * mm});
            skLineSegment(sketch, "E183.MirrorCS", {"start": v(-8.75, -166.56) * mm, "end": v(-7.88, -166.4) * mm});
            skArc(sketch, "E184.MirrorCS", {"start": v(-210.12, -35.79) * mm, "mid": v(-210.44, -35.7) * mm, "end": v(-210.62, -35.44) * mm});
            skLineSegment(sketch, "E185.MirrorCS", {"start": v(-78.06, -164.4) * mm, "end": v(-74.96, -164.94) * mm});
            skArc(sketch, "E186.MirrorCS", {"start": v(-214.68, -0.58) * mm, "mid": v(-214.98, -0.44) * mm, "end": v(-215.1, -0.15) * mm});
            skArc(sketch, "E187.MirrorCS", {"start": v(-198.75, -68.81) * mm, "mid": v(-199.08, -68.8) * mm, "end": v(-199.3, -68.55) * mm});
            skLineSegment(sketch, "E188.MirrorCS", {"start": v(47.82, -145.46) * mm, "end": v(48.58, -145.02) * mm});
            skArc(sketch, "E189.MirrorCS", {"start": v(43.99, -147.67) * mm, "mid": v(43.67, -147.72) * mm, "end": v(43.4, -147.55) * mm});
            skArc(sketch, "E190.MirrorCS", {"start": v(-83.3, -163.47) * mm, "mid": v(-83.57, -163.3) * mm, "end": v(-83.66, -163) * mm});
            skLineSegment(sketch, "E191.MirrorCS", {"start": v(-189.2, -91.5) * mm, "end": v(-185.93, -96.17) * mm});
            skArc(sketch, "E192.MirrorCS", {"start": v(96.34, -96.63) * mm, "mid": v(96.47, -96.92) * mm, "end": v(96.37, -97.22) * mm});
            skArc(sketch, "E193.MirrorCS", {"start": v(-191.53, -86.6) * mm, "mid": v(-192.18, -87.23) * mm, "end": v(-191.58, -86.55) * mm});
            skLineSegment(sketch, "E194.MirrorCS", {"start": v(-143.55, -138.2) * mm, "end": v(-138.34, -141.85) * mm});
            skArc(sketch, "E195.MirrorCS", {"start": v(-133.37, -144.25) * mm, "mid": v(-134.05, -144.84) * mm, "end": v(-133.42, -144.2) * mm});
            skLineSegment(sketch, "E196.MirrorCS", {"start": v(-202.2, -61.58) * mm, "end": v(-201.34, -63.63) * mm});
            skArc(sketch, "E197.MirrorCS", {"start": v(124.15, -40.67) * mm, "mid": v(124.38, -40.9) * mm, "end": v(124.4, -41.22) * mm});
            skArc(sketch, "E198.MirrorCS", {"start": v(-215.94, 16.63) * mm, "mid": v(-215.81, 16.97) * mm, "end": v(-215.48, 17.11) * mm});
            skLineSegment(sketch, "E199.MirrorCS", {"start": v(93.2, -101.26) * mm, "end": v(93.27, -101.18) * mm});
            skLineSegment(sketch, "E200.MirrorCS", {"start": v(122.78, -46.28) * mm, "end": v(122.8, -46.2) * mm});
            skLineSegment(sketch, "E201.MirrorCS", {"start": v(-109.6, -129.74) * mm, "end": v(-91.8, -137.34) * mm});
            skLineSegment(sketch, "E202.MirrorCS", {"start": v(88.8, -73.7) * mm, "end": v(96.25, -60.1) * mm});
            skLineSegment(sketch, "E203.MirrorCS", {"start": v(-184.28, -45.38) * mm, "end": v(-177, -62.29) * mm});
            skLineSegment(sketch, "E204.MirrorCS", {"start": v(-156.49, -93.03) * mm, "end": v(-142.97, -106.87) * mm});
            skLineSegment(sketch, "E205.MirrorCS", {"start": v(48.98, -116.76) * mm, "end": v(63.88, -104.35) * mm});
            skLineSegment(sketch, "E206.MirrorCS", {"start": v(29.72, -128.73) * mm, "end": v(43.07, -120.86) * mm});
            skLineSegment(sketch, "E207.MirrorCS", {"start": v(5.05, -139) * mm, "end": v(19.56, -133.57) * mm});
            skLineSegment(sketch, "E208.MirrorCS", {"start": v(-172.93, -69.84) * mm, "end": v(-160.25, -88.48) * mm});
            skLineSegment(sketch, "E209.MirrorCS", {"start": v(101.64, -47.59) * mm, "end": v(106.37, -32.83) * mm});
            skLineSegment(sketch, "E210.MirrorCS", {"start": v(-135.97, -112.81) * mm, "end": v(-116.9, -125.8) * mm});
            skLineSegment(sketch, "E211.MirrorCS", {"start": v(73.17, -94.73) * mm, "end": v(82.83, -82.64) * mm});
            skLineSegment(sketch, "E212.MirrorCS", {"start": v(-20.03, -144.65) * mm, "end": v(-4.82, -141.75) * mm});
            skLineSegment(sketch, "E213.MirrorCS", {"start": v(-129.9, -140.81) * mm, "end": v(-116.9, -125.8) * mm});
            skLineSegment(sketch, "E214.MirrorCS", {"start": v(63.2, -130.49) * mm, "end": v(48.98, -116.76) * mm});
            skLineSegment(sketch, "E215.MirrorCS", {"start": v(-188.16, -83.07) * mm, "end": v(-172.93, -69.84) * mm});
            skLineSegment(sketch, "E216.MirrorCS", {"start": v(107.88, -67.92) * mm, "end": v(96.25, -60.1) * mm});
            skLineSegment(sketch, "E217.MirrorCS", {"start": v(40.27, -143.25) * mm, "end": v(29.72, -128.73) * mm});
            skLineSegment(sketch, "E218.MirrorCS", {"start": v(92.77, -92.93) * mm, "end": v(82.83, -82.64) * mm});
            skLineSegment(sketch, "E219.MirrorCS", {"start": v(84.72, -102.52) * mm, "end": v(73.17, -94.73) * mm});
            skLineSegment(sketch, "E220.MirrorCS", {"start": v(-145.46, -129.93) * mm, "end": v(-135.97, -112.81) * mm});
            skLineSegment(sketch, "E221.MirrorCS", {"start": v(-157.25, -119.33) * mm, "end": v(-142.97, -106.87) * mm});
            skLineSegment(sketch, "E222.MirrorCS", {"start": v(74.87, -120.65) * mm, "end": v(63.88, -104.35) * mm});
            skLineSegment(sketch, "E223.MirrorCS", {"start": v(-168.4, -109.03) * mm, "end": v(-156.49, -93.03) * mm});
            skLineSegment(sketch, "E224.MirrorCS", {"start": v(-199.36, -53.57) * mm, "end": v(-184.28, -45.38) * mm});
            skLineSegment(sketch, "E225.MirrorCS", {"start": v(102, -79.02) * mm, "end": v(88.8, -73.7) * mm});
            skPoint(sketch, "E226.MirrorP", {"position": v(-171.8, -113.62) * mm});
            skPoint(sketch, "E227.MirrorP", {"position": v(78.03, -125.33) * mm});
            skPoint(sketch, "E228.MirrorP", {"position": v(-115.31, -152.67) * mm});
            skPoint(sketch, "E229.MirrorP", {"position": v(-3.11, -165.57) * mm});
            skPoint(sketch, "E230.MirrorP", {"position": v(96.62, -96.91) * mm});
            skLineSegment(sketch, "E231.MirrorCS", {"start": v(-113.93, -147.12) * mm, "end": v(-109.6, -129.74) * mm});
            skLineSegment(sketch, "E232.MirrorCS", {"start": v(-82.09, -140.42) * mm, "end": v(-63.13, -144.46) * mm});
            skLineSegment(sketch, "E233.MirrorCS", {"start": v(119.3, -38.53) * mm, "end": v(106.37, -32.83) * mm});
            skLineSegment(sketch, "E234.MirrorCS", {"start": v(-204.86, -35.17) * mm, "end": v(-188.1, -33.2) * mm});
            skLineSegment(sketch, "E235.MirrorCS", {"start": v(-67.76, -160.45) * mm, "end": v(-63.13, -144.46) * mm});
            skLineSegment(sketch, "E236.MirrorCS", {"start": v(123.34, -20) * mm, "end": v(109.24, -19.73) * mm});
            skPoint(sketch, "E237.MirrorP", {"position": v(43.63, -147.88) * mm});
            skLineSegment(sketch, "E238.MirrorCS", {"start": v(-3.52, -159.85) * mm, "end": v(-4.82, -141.75) * mm});
            skPoint(sketch, "E239.MirrorP", {"position": v(130.44, -8.84) * mm});
            skPoint(sketch, "E240.MirrorP", {"position": v(-69.34, -165.93) * mm});
            skPoint(sketch, "E241.MirrorP", {"position": v(52.77, -142.6) * mm});
            skPoint(sketch, "E242.MirrorP", {"position": v(124.53, -40.84) * mm});
            skLineSegment(sketch, "E243.MirrorCS", {"start": v(-83.3, -157.7) * mm, "end": v(-82.09, -140.42) * mm});
            skLineSegment(sketch, "E244.MirrorCS", {"start": v(-15.09, -161.9) * mm, "end": v(-20.03, -144.65) * mm});
            skLineSegment(sketch, "E245.MirrorCS", {"start": v(-191.8, -15.1) * mm, "end": v(-188.1, -33.2) * mm});
            skPoint(sketch, "E246.MirrorP", {"position": v(-35.64, -169.43) * mm});
            skPoint(sketch, "E247.MirrorP", {"position": v(-210.53, -35.84) * mm});
            skLineSegment(sketch, "E248.MirrorCS", {"start": v(-35.04, -163.74) * mm, "end": v(-33.16, -145.9) * mm});
            skPoint(sketch, "E249.MirrorP", {"position": v(-133.65, -145.14) * mm});
            skPoint(sketch, "E250.MirrorP", {"position": v(67.36, -134.5) * mm});
            skPoint(sketch, "E251.MirrorP", {"position": v(-83.7, -163.4) * mm});
            skPoint(sketch, "E252.MirrorP", {"position": v(-192.47, -86.83) * mm});
            skPoint(sketch, "E253.MirrorP", {"position": v(25.34, -156.65) * mm});
            skPoint(sketch, "E254.MirrorP", {"position": v(121.06, -51.64) * mm});
            skLineSegment(sketch, "E255.MirrorCS", {"start": v(-177.66, -98.1) * mm, "end": v(-160.25, -88.48) * mm});
            skLineSegment(sketch, "E256.MirrorCS", {"start": v(-46.79, -163.74) * mm, "end": v(-48.66, -145.9) * mm});
            skPoint(sketch, "E257.MirrorP", {"position": v(-161.54, -123.08) * mm});
            skLineSegment(sketch, "E258.MirrorCS", {"start": v(115.46, -50.47) * mm, "end": v(101.64, -47.59) * mm});
            skLineSegment(sketch, "E259.MirrorCS", {"start": v(12.92, -155.12) * mm, "end": v(5.05, -139) * mm});
            skPoint(sketch, "E260.MirrorP", {"position": v(112.71, -71.18) * mm});
            skPoint(sketch, "E261.MirrorP", {"position": v(89.62, -105.82) * mm});
            skLineSegment(sketch, "E262.MirrorCS", {"start": v(23.95, -151.1) * mm, "end": v(19.56, -133.57) * mm});
            skPoint(sketch, "E263.MirrorP", {"position": v(-199.14, -68.93) * mm});
            skLineSegment(sketch, "E264.MirrorCS", {"start": v(-99.27, -152.48) * mm, "end": v(-91.8, -137.34) * mm});
            skPoint(sketch, "E265.MirrorP", {"position": v(-182.65, -100.85) * mm});
            skLineSegment(sketch, "E266.MirrorCS", {"start": v(-193.65, -67.28) * mm, "end": v(-177, -62.29) * mm});
            skPoint(sketch, "E267.MirrorP", {"position": v(107.2, -81.1) * mm});
            skPoint(sketch, "E268.MirrorP", {"position": v(15.42, -160.26) * mm});
            skPoint(sketch, "E269.MirrorP", {"position": v(-13.51, -167.4) * mm});
            skPoint(sketch, "E270.MirrorP", {"position": v(129.08, -20.1) * mm});
            skLineSegment(sketch, "E271.MirrorCS", {"start": v(50.44, -137.37) * mm, "end": v(43.07, -120.86) * mm});
            skPoint(sketch, "E272.MirrorP", {"position": v(-101.78, -157.6) * mm});
            skPoint(sketch, "E273.MirrorP", {"position": v(-213.55, -22.51) * mm});
            skLineSegment(sketch, "E274.MirrorCS", {"start": v(-48.66, -145.9) * mm, "end": v(-33.16, -145.9) * mm});
            skPoint(sketch, "E275.MirrorP", {"position": v(-148.23, -134.93) * mm});
            skPoint(sketch, "E276.MirrorP", {"position": v(-46.19, -169.43) * mm});
            skLineSegment(sketch, "E277.MirrorCS", {"start": v(-208.14, -20.67) * mm, "end": v(-191.8, -15.1) * mm});
            skPoint(sketch, "E278.MirrorP", {"position": v(-204.38, -56.3) * mm});
            skLineSegment(sketch, "E279.MirrorCS", {"start": v(124.9, -7.55) * mm, "end": v(111.11, -4.35) * mm});
            skLineSegment(sketch, "E280.MirrorCS", {"start": v(109.24, -19.73) * mm, "end": v(111.11, -4.35) * mm});
            skLineSegment(sketch, "E281.MirrorCS", {"start": v(-215.63, 2.19) * mm, "end": v(-215.37, 7.49) * mm});
            skPoint(sketch, "E282.newPointA", {"position": v(252.74, -10.13) * mm});
            skPoint(sketch, "E282.newPointB", {"position": v(252.48, -10.68) * mm});
            skArc(sketch, "E282.filletArc", {"start": v(255.53, -8.97) * mm, "mid": v(253.56, -10.86) * mm, "end": v(253.35, -13.58) * mm});
            skPoint(sketch, "E283.newPointA", {"position": v(259.14, -7.9) * mm});
            skPoint(sketch, "E283.newPointB", {"position": v(258.57, -7.7) * mm});
            skArc(sketch, "E283.filletArc", {"start": v(260.6, -10.56) * mm, "mid": v(258.5, -8.79) * mm, "end": v(255.78, -8.87) * mm});
            skPoint(sketch, "E284.newPointA", {"position": v(229.92, -25.5) * mm});
            skPoint(sketch, "E284.newPointB", {"position": v(230, -24.9) * mm});
            skArc(sketch, "E284.filletArc", {"start": v(232.31, -22.96) * mm, "mid": v(231, -25.35) * mm, "end": v(231.6, -28) * mm});
            skPoint(sketch, "E285.newPointA", {"position": v(234.83, -20.85) * mm});
            skPoint(sketch, "E285.newPointB", {"position": v(239.04, -21.03) * mm});
            skArc(sketch, "E285.filletArc", {"start": v(239.8, -22.12) * mm, "mid": v(237.17, -20.5) * mm, "end": v(234.21, -21.37) * mm});
            skPoint(sketch, "E286.newPointA", {"position": v(277.58, -3.32) * mm});
            skPoint(sketch, "E286.newPointB", {"position": v(278, -2.88) * mm});
            skArc(sketch, "E286.filletArc", {"start": v(281, -2.62) * mm, "mid": v(278.55, -3.81) * mm, "end": v(277.53, -6.35) * mm});
            skPoint(sketch, "E287.newPointA", {"position": v(284.28, -2.33) * mm});
            skPoint(sketch, "E287.newPointB", {"position": v(284.77, -2.7) * mm});
            skArc(sketch, "E287.filletArc", {"start": v(285.35, -5.65) * mm, "mid": v(283.9, -3.34) * mm, "end": v(281.28, -2.6) * mm});
            skPoint(sketch, "E288.newPointA", {"position": v(302.38, -3.17) * mm});
            skPoint(sketch, "E288.newPointB", {"position": v(302.89, -2.85) * mm});
            skArc(sketch, "E288.filletArc", {"start": v(305.87, -3.37) * mm, "mid": v(303.19, -3.9) * mm, "end": v(301.54, -6.07) * mm});
            skPoint(sketch, "E289.newPointA", {"position": v(309.1, -3.94) * mm});
            skPoint(sketch, "E289.newPointB", {"position": v(309.48, -4.42) * mm});
            skArc(sketch, "E289.filletArc", {"start": v(309.27, -7.44) * mm, "mid": v(308.47, -4.83) * mm, "end": v(306.13, -3.42) * mm});
            skPoint(sketch, "E290.newPointA", {"position": v(327.83, -9.98) * mm});
            skPoint(sketch, "E290.newPointB", {"position": v(327.23, -10.15) * mm});
            skArc(sketch, "E290.filletArc", {"start": v(330.62, -11.41) * mm, "mid": v(327.84, -11.14) * mm, "end": v(325.62, -12.84) * mm});
            skPoint(sketch, "E291.newPointA", {"position": v(333.43, -12.85) * mm});
            skPoint(sketch, "E291.newPointB", {"position": v(333.65, -13.4) * mm});
            skArc(sketch, "E291.filletArc", {"start": v(332.7, -16.15) * mm, "mid": v(332.63, -13.49) * mm, "end": v(330.84, -11.52) * mm});
            skPoint(sketch, "E292.newPointA", {"position": v(349.15, -23.9) * mm});
            skPoint(sketch, "E292.newPointB", {"position": v(349.78, -23.9) * mm});
            skArc(sketch, "E292.filletArc", {"start": v(352.11, -26.2) * mm, "mid": v(349.46, -25.1) * mm, "end": v(346.8, -26.17) * mm});
            skPoint(sketch, "E293.newPointA", {"position": v(354.25, -28.3) * mm});
            skPoint(sketch, "E293.newPointB", {"position": v(354.3, -28.87) * mm});
            skArc(sketch, "E293.filletArc", {"start": v(352.74, -31.18) * mm, "mid": v(353.37, -28.67) * mm, "end": v(352.26, -26.34) * mm});
            skPoint(sketch, "E294.newPointA", {"position": v(369.9, -48.6) * mm});
            skPoint(sketch, "E294.newPointB", {"position": v(369.79, -49.2) * mm});
            skArc(sketch, "E294.filletArc", {"start": v(367.25, -51.04) * mm, "mid": v(368.75, -48.69) * mm, "end": v(368.24, -45.94) * mm});
            skPoint(sketch, "E295.newPointA", {"position": v(365.98, -43.06) * mm});
            skPoint(sketch, "E295.newPointB", {"position": v(366.55, -43.23) * mm});
            skArc(sketch, "E295.filletArc", {"start": v(368.1, -45.7) * mm, "mid": v(365.98, -44.08) * mm, "end": v(363.32, -44.24) * mm});
            skPoint(sketch, "E296.newPointA", {"position": v(377.9, -68.12) * mm});
            skPoint(sketch, "E296.newPointB", {"position": v(377.41, -67.78) * mm});
            skArc(sketch, "E296.filletArc", {"start": v(378.65, -70.95) * mm, "mid": v(377.1, -68.77) * mm, "end": v(374.5, -68.13) * mm});
            skPoint(sketch, "E297.newPointA", {"position": v(379.21, -74.78) * mm});
            skPoint(sketch, "E297.newPointB", {"position": v(379.5, -74.24) * mm});
            skArc(sketch, "E297.filletArc", {"start": v(376.26, -75.79) * mm, "mid": v(378.38, -73.99) * mm, "end": v(378.72, -71.22) * mm});
            skPoint(sketch, "E298.newPointA", {"position": v(211.63, -47.48) * mm});
            skPoint(sketch, "E298.newPointB", {"position": v(211.73, -48.08) * mm});
            skArc(sketch, "E298.filletArc", {"start": v(213.25, -44.93) * mm, "mid": v(212.71, -47.6) * mm, "end": v(214.1, -49.95) * mm});
            skPoint(sketch, "E299.newPointA", {"position": v(215.6, -41.99) * mm});
            skPoint(sketch, "E299.newPointB", {"position": v(215.01, -42.15) * mm});
            skArc(sketch, "E299.filletArc", {"start": v(218.3, -43.33) * mm, "mid": v(215.59, -43.07) * mm, "end": v(213.4, -44.7) * mm});
            skPoint(sketch, "E300.newPointA", {"position": v(203.58, -67.73) * mm});
            skPoint(sketch, "E300.newPointB", {"position": v(203.08, -68.06) * mm});
            skArc(sketch, "E300.filletArc", {"start": v(206.56, -68.2) * mm, "mid": v(203.9, -68.77) * mm, "end": v(202.3, -70.97) * mm});
            skPoint(sketch, "E301.newPointA", {"position": v(201.44, -74.16) * mm});
            skPoint(sketch, "E301.newPointB", {"position": v(201.72, -74.7) * mm});
            skArc(sketch, "E301.filletArc", {"start": v(202.22, -71.24) * mm, "mid": v(202.5, -73.96) * mm, "end": v(204.54, -75.78) * mm});
            skPoint(sketch, "E302.newPointA", {"position": v(229.92, -160.46) * mm});
            skPoint(sketch, "E302.newPointB", {"position": v(230, -161.06) * mm});
            skArc(sketch, "E302.filletArc", {"start": v(231.6, -157.96) * mm, "mid": v(231, -160.62) * mm, "end": v(232.31, -163) * mm});
            skLineSegment(sketch, "E303.bottom", {"start": v(201.47, -111.8) * mm, "end": v(201.43, -111.57) * mm});
            skLineSegment(sketch, "E303.top", {"start": v(217.2, -114.13) * mm, "end": v(215.03, -104.1) * mm});
            skLineSegment(sketch, "E303.left", {"start": v(205.49, -114.95) * mm, "end": v(217.2, -114.13) * mm});
            skLineSegment(sketch, "E303.right", {"start": v(204.12, -107.25) * mm, "end": v(215.03, -104.1) * mm});
            skPoint(sketch, "E304.visualSharp", {"position": v(202.07, -115.19) * mm});
            skArc(sketch, "E304.filletArc", {"start": v(202, -114.78) * mm, "mid": v(202.16, -115.06) * mm, "end": v(202.47, -115.16) * mm});
            skPoint(sketch, "E305.visualSharp", {"position": v(200.83, -108.2) * mm});
            skArc(sketch, "E305.filletArc", {"start": v(201.23, -108.09) * mm, "mid": v(200.97, -108.29) * mm, "end": v(200.9, -108.6) * mm});
            skPoint(sketch, "E306.newPointA", {"position": v(201.23, -108.09) * mm});
            skPoint(sketch, "E306.newPointB", {"position": v(200.9, -108.6) * mm});
            skArc(sketch, "E306.filletArc", {"start": v(204.12, -107.25) * mm, "mid": v(201.95, -108.9) * mm, "end": v(201.43, -111.57) * mm});
            skPoint(sketch, "E307.newPointA", {"position": v(202, -114.82) * mm});
            skPoint(sketch, "E307.newPointB", {"position": v(202.65, -115.15) * mm});
            skArc(sketch, "E307.filletArc", {"start": v(201.47, -111.8) * mm, "mid": v(202.88, -114.15) * mm, "end": v(205.49, -114.95) * mm});
            skLineSegment(sketch, "E308.bottom", {"start": v(211.9, -138.97) * mm, "end": v(211.83, -138.85) * mm});
            skLineSegment(sketch, "E308.top", {"start": v(227.77, -136.36) * mm, "end": v(222.54, -127.62) * mm});
            skLineSegment(sketch, "E308.left", {"start": v(216.67, -140.75) * mm, "end": v(227.77, -136.36) * mm});
            skLineSegment(sketch, "E308.right", {"start": v(213.1, -133.92) * mm, "end": v(222.54, -127.62) * mm});
            skPoint(sketch, "E309.visualSharp", {"position": v(213.48, -142) * mm});
            skArc(sketch, "E309.filletArc", {"start": v(213.3, -141.65) * mm, "mid": v(213.53, -141.86) * mm, "end": v(213.86, -141.86) * mm});
            skPoint(sketch, "E310.visualSharp", {"position": v(210.25, -135.82) * mm});
            skArc(sketch, "E310.filletArc", {"start": v(210.59, -135.6) * mm, "mid": v(210.4, -135.86) * mm, "end": v(210.44, -136.18) * mm});
            skPoint(sketch, "E311.newPointA", {"position": v(210.59, -135.6) * mm});
            skPoint(sketch, "E311.newPointB", {"position": v(210.44, -136.18) * mm});
            skArc(sketch, "E311.filletArc", {"start": v(213.1, -133.92) * mm, "mid": v(211.52, -136.14) * mm, "end": v(211.83, -138.85) * mm});
            skPoint(sketch, "E312.newPointA", {"position": v(213.36, -141.78) * mm});
            skPoint(sketch, "E312.newPointB", {"position": v(214.2, -141.73) * mm});
            skArc(sketch, "E312.filletArc", {"start": v(211.9, -138.97) * mm, "mid": v(213.94, -140.77) * mm, "end": v(216.67, -140.75) * mm});
            skPoint(sketch, "E313.newPointA", {"position": v(234.83, -165.12) * mm});
            skPoint(sketch, "E313.newPointB", {"position": v(239.04, -164.93) * mm});
            skArc(sketch, "E313.filletArc", {"start": v(234.21, -164.6) * mm, "mid": v(237.17, -165.46) * mm, "end": v(239.8, -163.85) * mm});
            skPoint(sketch, "E314.newPointA", {"position": v(252.48, -175.28) * mm});
            skPoint(sketch, "E314.newPointB", {"position": v(252.74, -175.83) * mm});
            skArc(sketch, "E314.filletArc", {"start": v(253.35, -172.39) * mm, "mid": v(253.56, -175.11) * mm, "end": v(255.53, -177) * mm});
            skPoint(sketch, "E315.newPointA", {"position": v(258.57, -178.26) * mm});
            skPoint(sketch, "E315.newPointB", {"position": v(259.14, -178.06) * mm});
            skArc(sketch, "E315.filletArc", {"start": v(255.78, -177.1) * mm, "mid": v(258.5, -177.18) * mm, "end": v(260.6, -175.4) * mm});
            skPoint(sketch, "E316.newPointA", {"position": v(277.58, -182.64) * mm});
            skPoint(sketch, "E316.newPointB", {"position": v(278, -183.08) * mm});
            skArc(sketch, "E316.filletArc", {"start": v(277.53, -179.62) * mm, "mid": v(278.55, -182.15) * mm, "end": v(281, -183.35) * mm});
            skPoint(sketch, "E317.newPointA", {"position": v(284.28, -183.64) * mm});
            skPoint(sketch, "E317.newPointB", {"position": v(284.77, -183.27) * mm});
            skArc(sketch, "E317.filletArc", {"start": v(281.28, -183.37) * mm, "mid": v(283.9, -182.62) * mm, "end": v(285.35, -180.31) * mm});
            skPoint(sketch, "E318.newPointA", {"position": v(302.89, -183.12) * mm});
            skPoint(sketch, "E318.newPointB", {"position": v(302.38, -182.8) * mm});
            skArc(sketch, "E318.filletArc", {"start": v(301.54, -179.9) * mm, "mid": v(303.19, -182.07) * mm, "end": v(305.87, -182.6) * mm});
            skPoint(sketch, "E319.newPointA", {"position": v(309.1, -182.02) * mm});
            skPoint(sketch, "E319.newPointB", {"position": v(309.48, -181.54) * mm});
            skArc(sketch, "E319.filletArc", {"start": v(306.13, -182.55) * mm, "mid": v(308.47, -181.14) * mm, "end": v(309.27, -178.53) * mm});
            skPoint(sketch, "E320.newPointA", {"position": v(327.83, -175.99) * mm});
            skPoint(sketch, "E320.newPointB", {"position": v(327.23, -175.82) * mm});
            skArc(sketch, "E320.filletArc", {"start": v(325.62, -173.13) * mm, "mid": v(327.84, -174.83) * mm, "end": v(330.62, -174.56) * mm});
            skPoint(sketch, "E321.newPointA", {"position": v(333.43, -173.12) * mm});
            skPoint(sketch, "E321.newPointB", {"position": v(333.65, -172.57) * mm});
            skArc(sketch, "E321.filletArc", {"start": v(330.84, -174.44) * mm, "mid": v(332.63, -172.48) * mm, "end": v(332.7, -169.81) * mm});
            skPoint(sketch, "E322.newPointA", {"position": v(349.78, -162.06) * mm});
            skPoint(sketch, "E322.newPointB", {"position": v(349.15, -162.07) * mm});
            skArc(sketch, "E322.filletArc", {"start": v(346.8, -159.8) * mm, "mid": v(349.46, -160.86) * mm, "end": v(352.11, -159.77) * mm});
            skPoint(sketch, "E323.newPointA", {"position": v(354.25, -157.67) * mm});
            skPoint(sketch, "E323.newPointB", {"position": v(354.3, -157.1) * mm});
            skArc(sketch, "E323.filletArc", {"start": v(352.26, -159.63) * mm, "mid": v(353.37, -157.3) * mm, "end": v(352.74, -154.78) * mm});
            skPoint(sketch, "E324.newPointA", {"position": v(366.55, -142.74) * mm});
            skPoint(sketch, "E324.newPointB", {"position": v(365.98, -142.91) * mm});
            skArc(sketch, "E324.filletArc", {"start": v(363.32, -141.72) * mm, "mid": v(365.98, -141.89) * mm, "end": v(368.1, -140.26) * mm});
            skPoint(sketch, "E325.newPointA", {"position": v(369.9, -137.37) * mm});
            skPoint(sketch, "E325.newPointB", {"position": v(369.79, -136.76) * mm});
            skArc(sketch, "E325.filletArc", {"start": v(368.24, -140.03) * mm, "mid": v(368.75, -137.28) * mm, "end": v(367.25, -134.92) * mm});
            skPoint(sketch, "E326.newPointA", {"position": v(377.41, -118.18) * mm});
            skPoint(sketch, "E326.newPointB", {"position": v(377.9, -117.85) * mm});
            skArc(sketch, "E326.filletArc", {"start": v(374.5, -117.83) * mm, "mid": v(377.1, -117.2) * mm, "end": v(378.65, -115.01) * mm});
            skPoint(sketch, "E327.newPointA", {"position": v(379.5, -111.73) * mm});
            skPoint(sketch, "E327.newPointB", {"position": v(379.21, -111.18) * mm});
            skArc(sketch, "E327.filletArc", {"start": v(378.72, -114.74) * mm, "mid": v(378.38, -111.98) * mm, "end": v(376.26, -110.18) * mm});
            skPoint(sketch, "E328.newPointA", {"position": v(-111.7, 166.6) * mm});
            skPoint(sketch, "E328.newPointB", {"position": v(-113.54, 158.18) * mm});
            skArc(sketch, "E328.filletArc", {"start": v(-109.94, 167.25) * mm, "mid": v(-113.37, 164.26) * mm, "end": v(-113.93, 159.74) * mm});
            skPoint(sketch, "E329.newPointA", {"position": v(-100.21, 167.02) * mm});
            skPoint(sketch, "E329.newPointB", {"position": v(-101.84, 170.2) * mm});
            skArc(sketch, "E329.filletArc", {"start": v(-99.27, 165.1) * mm, "mid": v(-102.6, 168.2) * mm, "end": v(-107.13, 168.27) * mm});
            skPoint(sketch, "E330.newPointA", {"position": v(-79.52, 176.76) * mm});
            skPoint(sketch, "E330.newPointB", {"position": v(-83.4, 171.8) * mm});
            skArc(sketch, "E330.filletArc", {"start": v(-78.06, 177.02) * mm, "mid": v(-81.96, 174.68) * mm, "end": v(-83.3, 170.32) * mm});
            skPoint(sketch, "E331.newPointA", {"position": v(-69.74, 178.49) * mm});
            skPoint(sketch, "E331.newPointB", {"position": v(-69.23, 178.17) * mm});
            skArc(sketch, "E331.filletArc", {"start": v(-67.76, 173.08) * mm, "mid": v(-70.5, 176.7) * mm, "end": v(-74.96, 177.57) * mm});
            skPoint(sketch, "E332.newPointA", {"position": v(-41.96, 182.05) * mm});
            skPoint(sketch, "E332.newPointB", {"position": v(-46.63, 177.84) * mm});
            skArc(sketch, "E332.filletArc", {"start": v(-40.47, 182.05) * mm, "mid": v(-44.72, 180.42) * mm, "end": v(-46.79, 176.36) * mm});
            skPoint(sketch, "E333.newPointA", {"position": v(-31.42, 182.05) * mm});
            skPoint(sketch, "E333.newPointB", {"position": v(-35.2, 177.84) * mm});
            skArc(sketch, "E333.filletArc", {"start": v(-35.04, 176.36) * mm, "mid": v(-37.1, 180.42) * mm, "end": v(-41.36, 182.05) * mm});
            skPoint(sketch, "E334.newPointA", {"position": v(-9.34, 179.29) * mm});
            skPoint(sketch, "E334.newPointB", {"position": v(-14.68, 175.95) * mm});
            skArc(sketch, "E334.filletArc", {"start": v(-7.88, 179.03) * mm, "mid": v(-12.35, 178.16) * mm, "end": v(-15.09, 174.53) * mm});
            skPoint(sketch, "E335.newPointA", {"position": v(1.03, 177.46) * mm});
            skPoint(sketch, "E335.newPointB", {"position": v(-3.42, 173.97) * mm});
            skArc(sketch, "E335.filletArc", {"start": v(-3.52, 172.48) * mm, "mid": v(-4.85, 176.84) * mm, "end": v(-8.75, 179.18) * mm});
            skPoint(sketch, "E336.newPointA", {"position": v(19.4, 171.44) * mm});
            skPoint(sketch, "E336.newPointB", {"position": v(13.57, 169.08) * mm});
            skArc(sketch, "E336.filletArc", {"start": v(20.8, 170.93) * mm, "mid": v(16.25, 170.85) * mm, "end": v(12.92, 167.75) * mm});
            skPoint(sketch, "E337.newPointA", {"position": v(29.3, 167.83) * mm});
            skPoint(sketch, "E337.newPointB", {"position": v(24.31, 165.17) * mm});
            skArc(sketch, "E337.filletArc", {"start": v(23.95, 163.72) * mm, "mid": v(23.4, 168.24) * mm, "end": v(19.96, 171.23) * mm});
            skPoint(sketch, "E338.newPointA", {"position": v(47.3, 158.38) * mm});
            skPoint(sketch, "E338.newPointB", {"position": v(41.14, 157.07) * mm});
            skArc(sketch, "E338.filletArc", {"start": v(48.58, 157.64) * mm, "mid": v(44.09, 158.35) * mm, "end": v(40.27, 155.87) * mm});
            skPoint(sketch, "E339.newPointA", {"position": v(56.42, 153.11) * mm});
            skPoint(sketch, "E339.newPointB", {"position": v(51.05, 151.36) * mm});
            skArc(sketch, "E339.filletArc", {"start": v(50.44, 150) * mm, "mid": v(50.68, 154.54) * mm, "end": v(47.82, 158.08) * mm});
            skPoint(sketch, "E340.newPointA", {"position": v(70.23, 144.66) * mm});
            skPoint(sketch, "E340.newPointB", {"position": v(60.35, 140.37) * mm});
            skArc(sketch, "E340.filletArc", {"start": v(64.56, 144.12) * mm, "mid": v(63.84, 143.66) * mm, "end": v(63.2, 143.11) * mm});
            skPoint(sketch, "E341.newPointA", {"position": v(78.2, 137.8) * mm});
            skPoint(sketch, "E341.newPointB", {"position": v(74.74, 133.08) * mm});
            skArc(sketch, "E341.filletArc", {"start": v(74.87, 133.27) * mm, "mid": v(75.13, 133.68) * mm, "end": v(75.35, 134.11) * mm});
            skPoint(sketch, "E342.newPointA", {"position": v(89.88, 118.12) * mm});
            skPoint(sketch, "E342.newPointB", {"position": v(89.27, 118.21) * mm});
            skArc(sketch, "E342.filletArc", {"start": v(93.27, 113.8) * mm, "mid": v(89.26, 116.15) * mm, "end": v(84.72, 115.14) * mm});
            skPoint(sketch, "E343.newPointA", {"position": v(96.37, 109.84) * mm});
            skPoint(sketch, "E343.newPointB", {"position": v(96.34, 109.25) * mm});
            skArc(sketch, "E343.filletArc", {"start": v(92.77, 105.56) * mm, "mid": v(94.55, 109.64) * mm, "end": v(93.2, 113.89) * mm});
            skPoint(sketch, "E344.newPointA", {"position": v(107.4, 93.38) * mm});
            skPoint(sketch, "E344.newPointB", {"position": v(106.83, 93.58) * mm});
            skArc(sketch, "E344.filletArc", {"start": v(109.92, 88.83) * mm, "mid": v(106.49, 91.73) * mm, "end": v(102, 91.64) * mm});
            skPoint(sketch, "E345.newPointA", {"position": v(112.51, 84.17) * mm});
            skPoint(sketch, "E345.newPointB", {"position": v(112.37, 83.57) * mm});
            skArc(sketch, "E345.filletArc", {"start": v(107.88, 80.55) * mm, "mid": v(110.5, 84.33) * mm, "end": v(109.88, 88.9) * mm});
            skPoint(sketch, "E346.newPointA", {"position": v(121.18, 63.88) * mm});
            skPoint(sketch, "E346.newPointB", {"position": v(120.66, 64.18) * mm});
            skArc(sketch, "E346.filletArc", {"start": v(122.8, 58.82) * mm, "mid": v(119.95, 62.37) * mm, "end": v(115.46, 63.1) * mm});
            skPoint(sketch, "E347.newPointA", {"position": v(124.4, 53.85) * mm});
            skPoint(sketch, "E347.newPointB", {"position": v(124.15, 53.3) * mm});
            skArc(sketch, "E347.filletArc", {"start": v(119.3, 51.15) * mm, "mid": v(122.52, 54.36) * mm, "end": v(122.78, 58.9) * mm});
            skPoint(sketch, "E348.newPointA", {"position": v(128.67, 32.72) * mm});
            skPoint(sketch, "E348.newPointB", {"position": v(129.13, 32.33) * mm});
            skArc(sketch, "E348.filletArc", {"start": v(129.77, 27.03) * mm, "mid": v(127.63, 31.06) * mm, "end": v(123.34, 32.62) * mm});
            skPoint(sketch, "E349.newPointA", {"position": v(130.39, 21.87) * mm});
            skPoint(sketch, "E349.newPointB", {"position": v(130.04, 21.37) * mm});
            skArc(sketch, "E349.filletArc", {"start": v(124.9, 20.17) * mm, "mid": v(128.65, 22.72) * mm, "end": v(129.76, 27.12) * mm});
            skPoint(sketch, "E350.newPointA", {"position": v(130.04, -8.75) * mm});
            skPoint(sketch, "E350.newPointB", {"position": v(130.39, -9.24) * mm});
            skArc(sketch, "E350.filletArc", {"start": v(129.76, -14.5) * mm, "mid": v(128.65, -10.1) * mm, "end": v(124.9, -7.55) * mm});
            skPoint(sketch, "E351.newPointA", {"position": v(129.13, -19.7) * mm});
            skPoint(sketch, "E351.newPointB", {"position": v(128.67, -20.1) * mm});
            skArc(sketch, "E351.filletArc", {"start": v(123.34, -20) * mm, "mid": v(127.63, -18.44) * mm, "end": v(129.77, -14.4) * mm});
            skPoint(sketch, "E352.newPointA", {"position": v(124.4, -41.22) * mm});
            skPoint(sketch, "E352.newPointB", {"position": v(124.15, -40.67) * mm});
            skArc(sketch, "E352.filletArc", {"start": v(122.78, -46.28) * mm, "mid": v(122.52, -41.74) * mm, "end": v(119.3, -38.53) * mm});
            skPoint(sketch, "E353.newPointA", {"position": v(121.18, -51.26) * mm});
            skPoint(sketch, "E353.newPointB", {"position": v(120.66, -51.56) * mm});
            skArc(sketch, "E353.filletArc", {"start": v(115.46, -50.47) * mm, "mid": v(119.95, -49.75) * mm, "end": v(122.8, -46.2) * mm});
            skPoint(sketch, "E354.newPointA", {"position": v(112.51, -71.54) * mm});
            skPoint(sketch, "E354.newPointB", {"position": v(112.37, -70.95) * mm});
            skArc(sketch, "E354.filletArc", {"start": v(109.88, -76.28) * mm, "mid": v(110.5, -71.7) * mm, "end": v(107.88, -67.92) * mm});
            skPoint(sketch, "E355.newPointA", {"position": v(106.83, -80.96) * mm});
            skPoint(sketch, "E355.newPointB", {"position": v(107.4, -80.76) * mm});
            skArc(sketch, "E355.filletArc", {"start": v(102, -79.02) * mm, "mid": v(106.49, -79.11) * mm, "end": v(109.92, -76.2) * mm});
            skPoint(sketch, "E356.newPointA", {"position": v(96.34, -96.63) * mm});
            skPoint(sketch, "E356.newPointB", {"position": v(96.37, -97.22) * mm});
            skArc(sketch, "E356.filletArc", {"start": v(93.2, -101.26) * mm, "mid": v(94.55, -97.02) * mm, "end": v(92.77, -92.93) * mm});
            skPoint(sketch, "E357.newPointA", {"position": v(89.27, -105.59) * mm});
            skPoint(sketch, "E357.newPointB", {"position": v(89.88, -105.5) * mm});
            skArc(sketch, "E357.filletArc", {"start": v(84.72, -102.52) * mm, "mid": v(89.26, -103.53) * mm, "end": v(93.27, -101.18) * mm});
            skPoint(sketch, "E358.newPointA", {"position": v(74.74, -120.46) * mm});
            skPoint(sketch, "E358.newPointB", {"position": v(78.2, -125.17) * mm});
            skArc(sketch, "E358.filletArc", {"start": v(73.75, -129) * mm, "mid": v(75.9, -125.04) * mm, "end": v(74.87, -120.65) * mm});
            skPoint(sketch, "E359.newPointA", {"position": v(70.23, -132.04) * mm});
            skPoint(sketch, "E359.newPointB", {"position": v(60.35, -127.74) * mm});
            skArc(sketch, "E359.filletArc", {"start": v(63.2, -130.49) * mm, "mid": v(67.42, -132.27) * mm, "end": v(71.75, -130.73) * mm});
            skPoint(sketch, "E360.newPointA", {"position": v(51.05, -138.73) * mm});
            skPoint(sketch, "E360.newPointB", {"position": v(56.42, -140.5) * mm});
            skArc(sketch, "E360.filletArc", {"start": v(47.82, -145.46) * mm, "mid": v(50.68, -141.92) * mm, "end": v(50.44, -137.37) * mm});
            skPoint(sketch, "E361.newPointA", {"position": v(47.3, -145.76) * mm});
            skPoint(sketch, "E361.newPointB", {"position": v(41.14, -144.45) * mm});
            skArc(sketch, "E361.filletArc", {"start": v(40.27, -143.25) * mm, "mid": v(44.09, -145.73) * mm, "end": v(48.58, -145.02) * mm});
            skPoint(sketch, "E362.newPointA", {"position": v(24.31, -152.55) * mm});
            skPoint(sketch, "E362.newPointB", {"position": v(29.3, -155.21) * mm});
            skArc(sketch, "E362.filletArc", {"start": v(19.96, -158.61) * mm, "mid": v(23.4, -155.62) * mm, "end": v(23.95, -151.1) * mm});
            skPoint(sketch, "E363.newPointA", {"position": v(19.4, -158.81) * mm});
            skPoint(sketch, "E363.newPointB", {"position": v(13.57, -156.46) * mm});
            skArc(sketch, "E363.filletArc", {"start": v(12.92, -155.12) * mm, "mid": v(16.25, -158.23) * mm, "end": v(20.8, -158.3) * mm});
            skPoint(sketch, "E364.newPointA", {"position": v(-3.42, -161.34) * mm});
            skPoint(sketch, "E364.newPointB", {"position": v(1.03, -164.84) * mm});
            skArc(sketch, "E364.filletArc", {"start": v(-8.75, -166.56) * mm, "mid": v(-4.85, -164.21) * mm, "end": v(-3.52, -159.85) * mm});
            skPoint(sketch, "E365.newPointA", {"position": v(-9.34, -166.66) * mm});
            skPoint(sketch, "E365.newPointB", {"position": v(-14.68, -163.33) * mm});
            skArc(sketch, "E365.filletArc", {"start": v(-15.09, -161.9) * mm, "mid": v(-12.35, -165.54) * mm, "end": v(-7.88, -166.4) * mm});
            skPoint(sketch, "E366.newPointA", {"position": v(-35.2, -165.22) * mm});
            skPoint(sketch, "E366.newPointB", {"position": v(-31.42, -169.43) * mm});
            skArc(sketch, "E366.filletArc", {"start": v(-41.36, -169.43) * mm, "mid": v(-37.1, -167.8) * mm, "end": v(-35.04, -163.74) * mm});
            skPoint(sketch, "E367.newPointA", {"position": v(-41.96, -169.43) * mm});
            skPoint(sketch, "E367.newPointB", {"position": v(-46.63, -165.22) * mm});
            skArc(sketch, "E367.filletArc", {"start": v(-46.79, -163.74) * mm, "mid": v(-44.72, -167.8) * mm, "end": v(-40.47, -169.43) * mm});
            skPoint(sketch, "E368.newPointA", {"position": v(-83.4, -159.18) * mm});
            skPoint(sketch, "E368.newPointB", {"position": v(-79.52, -164.14) * mm});
            skArc(sketch, "E368.filletArc", {"start": v(-83.3, -157.7) * mm, "mid": v(-81.96, -162.05) * mm, "end": v(-78.06, -164.4) * mm});
            skPoint(sketch, "E369.newPointA", {"position": v(-69.74, -165.86) * mm});
            skPoint(sketch, "E369.newPointB", {"position": v(-69.23, -165.54) * mm});
            skArc(sketch, "E369.filletArc", {"start": v(-74.96, -164.94) * mm, "mid": v(-70.5, -164.08) * mm, "end": v(-67.76, -160.45) * mm});
            skPoint(sketch, "E370.newPointA", {"position": v(-100.21, -154.4) * mm});
            skPoint(sketch, "E370.newPointB", {"position": v(-101.84, -157.57) * mm});
            skArc(sketch, "E370.filletArc", {"start": v(-107.13, -155.64) * mm, "mid": v(-102.6, -155.57) * mm, "end": v(-99.27, -152.48) * mm});
            skPoint(sketch, "E371.newPointA", {"position": v(-111.7, -153.98) * mm});
            skPoint(sketch, "E371.newPointB", {"position": v(-113.54, -145.56) * mm});
            skArc(sketch, "E371.filletArc", {"start": v(-113.93, -147.12) * mm, "mid": v(-113.37, -151.64) * mm, "end": v(-109.94, -154.62) * mm});
            skPoint(sketch, "E372.newPointA", {"position": v(-129.94, -140.86) * mm});
            skPoint(sketch, "E372.newPointB", {"position": v(-133.54, -145.22) * mm});
            skArc(sketch, "E372.filletArc", {"start": v(-138.34, -141.85) * mm, "mid": v(-133.92, -142.95) * mm, "end": v(-129.9, -140.81) * mm});
            skPoint(sketch, "E373.newPointA", {"position": v(-148.35, -134.85) * mm});
            skPoint(sketch, "E373.newPointB", {"position": v(-145.48, -129.97) * mm});
            skArc(sketch, "E373.filletArc", {"start": v(-145.46, -129.93) * mm, "mid": v(-146.1, -134.43) * mm, "end": v(-143.55, -138.2) * mm});
            skPoint(sketch, "E374.newPointA", {"position": v(-157.15, -119.24) * mm});
            skPoint(sketch, "E374.newPointB", {"position": v(-161.4, -123.2) * mm});
            skArc(sketch, "E374.filletArc", {"start": v(-165.73, -119.22) * mm, "mid": v(-161.51, -120.9) * mm, "end": v(-157.25, -119.33) * mm});
            skPoint(sketch, "E375.newPointA", {"position": v(-171.7, -113.71) * mm});
            skPoint(sketch, "E375.newPointB", {"position": v(-170.07, -111.28) * mm});
            skArc(sketch, "E375.filletArc", {"start": v(-168.4, -109.03) * mm, "mid": v(-169.62, -113.41) * mm, "end": v(-167.6, -117.5) * mm});
            skPoint(sketch, "E376.newPointA", {"position": v(-182.53, -101.02) * mm});
            skPoint(sketch, "E376.newPointB", {"position": v(-177.21, -97.85) * mm});
            skArc(sketch, "E376.filletArc", {"start": v(-185.93, -96.17) * mm, "mid": v(-182.16, -98.72) * mm, "end": v(-177.66, -98.1) * mm});
            skPoint(sketch, "E377.newPointA", {"position": v(-190.22, -84.87) * mm});
            skPoint(sketch, "E377.newPointB", {"position": v(-190.73, -89.3) * mm});
            skArc(sketch, "E377.filletArc", {"start": v(-188.16, -83.07) * mm, "mid": v(-190.3, -87.1) * mm, "end": v(-189.2, -91.5) * mm});
            skPoint(sketch, "E378.newPointA", {"position": v(-195.95, -67.97) * mm});
            skPoint(sketch, "E378.newPointB", {"position": v(-199.19, -68.83) * mm});
            skArc(sketch, "E378.filletArc", {"start": v(-201.34, -63.63) * mm, "mid": v(-198.2, -66.94) * mm, "end": v(-193.65, -67.28) * mm});
            skPoint(sketch, "E379.newPointA", {"position": v(-201.45, -54.7) * mm});
            skPoint(sketch, "E379.newPointB", {"position": v(-204.34, -56.4) * mm});
            skArc(sketch, "E379.filletArc", {"start": v(-199.36, -53.57) * mm, "mid": v(-202.31, -57.03) * mm, "end": v(-202.2, -61.58) * mm});
            skPoint(sketch, "E380.newPointA", {"position": v(-207.22, -35.45) * mm});
            skPoint(sketch, "E380.newPointB", {"position": v(-210.55, -35.74) * mm});
            skArc(sketch, "E380.filletArc", {"start": v(-211.8, -30.27) * mm, "mid": v(-209.26, -34.05) * mm, "end": v(-204.86, -35.17) * mm});
            skPoint(sketch, "E381.newPointA", {"position": v(-213.17, -22.38) * mm});
            skPoint(sketch, "E381.newPointB", {"position": v(-213.46, -22.91) * mm});
            skArc(sketch, "E381.filletArc", {"start": v(-208.14, -20.67) * mm, "mid": v(-211.64, -23.58) * mm, "end": v(-212.29, -28.09) * mm});
            skPoint(sketch, "E382.newPointA", {"position": v(-129.94, 153.48) * mm});
            skPoint(sketch, "E382.newPointB", {"position": v(-133.54, 157.84) * mm});
            skArc(sketch, "E382.filletArc", {"start": v(-129.9, 153.43) * mm, "mid": v(-133.92, 155.58) * mm, "end": v(-138.34, 154.48) * mm});
            skPoint(sketch, "E383.newPointA", {"position": v(-145.48, 142.6) * mm});
            skPoint(sketch, "E383.newPointB", {"position": v(-148.35, 147.47) * mm});
            skArc(sketch, "E383.filletArc", {"start": v(-143.55, 150.83) * mm, "mid": v(-146.1, 147.06) * mm, "end": v(-145.46, 142.55) * mm});
            skPoint(sketch, "E384.newPointA", {"position": v(-161.4, 135.83) * mm});
            skPoint(sketch, "E384.newPointB", {"position": v(-157.15, 131.87) * mm});
            skArc(sketch, "E384.filletArc", {"start": v(-157.25, 131.96) * mm, "mid": v(-161.51, 133.52) * mm, "end": v(-165.73, 131.84) * mm});
            skPoint(sketch, "E385.newPointA", {"position": v(-171.7, 126.34) * mm});
            skPoint(sketch, "E385.newPointB", {"position": v(-170.07, 123.9) * mm});
            skArc(sketch, "E385.filletArc", {"start": v(-167.6, 130.11) * mm, "mid": v(-169.62, 126.04) * mm, "end": v(-168.4, 121.65) * mm});
            skPoint(sketch, "E386.newPointA", {"position": v(-177.21, 110.47) * mm});
            skPoint(sketch, "E386.newPointB", {"position": v(-182.53, 113.64) * mm});
            skArc(sketch, "E386.filletArc", {"start": v(-177.66, 110.71) * mm, "mid": v(-182.16, 111.34) * mm, "end": v(-185.93, 108.8) * mm});
            skPoint(sketch, "E387.newPointA", {"position": v(-190.73, 101.93) * mm});
            skPoint(sketch, "E387.newPointB", {"position": v(-190.22, 97.49) * mm});
            skArc(sketch, "E387.filletArc", {"start": v(-189.2, 104.13) * mm, "mid": v(-190.3, 99.72) * mm, "end": v(-188.16, 95.7) * mm});
            skPoint(sketch, "E388.newPointA", {"position": v(-195.95, 80.6) * mm});
            skPoint(sketch, "E388.newPointB", {"position": v(-199.19, 81.45) * mm});
            skArc(sketch, "E388.filletArc", {"start": v(-193.65, 79.9) * mm, "mid": v(-198.2, 79.56) * mm, "end": v(-201.34, 76.26) * mm});
            skPoint(sketch, "E389.newPointA", {"position": v(-201.45, 67.33) * mm});
            skPoint(sketch, "E389.newPointB", {"position": v(-204.34, 69.02) * mm});
            skArc(sketch, "E389.filletArc", {"start": v(-202.2, 74.2) * mm, "mid": v(-202.31, 69.66) * mm, "end": v(-199.36, 66.2) * mm});
            skPoint(sketch, "E390.newPointA", {"position": v(-210.55, 48.36) * mm});
            skPoint(sketch, "E390.newPointB", {"position": v(-207.22, 48.07) * mm});
            skArc(sketch, "E390.filletArc", {"start": v(-204.86, 47.8) * mm, "mid": v(-209.26, 46.67) * mm, "end": v(-211.8, 42.9) * mm});
            skPoint(sketch, "E391.newPointA", {"position": v(-213.17, 35) * mm});
            skPoint(sketch, "E391.newPointB", {"position": v(-213.46, 35.53) * mm});
            skArc(sketch, "E391.filletArc", {"start": v(-212.29, 40.71) * mm, "mid": v(-211.64, 36.2) * mm, "end": v(-208.14, 33.3) * mm});
            skPoint(sketch, "E392.newPointA", {"position": v(-214.68, 13.2) * mm});
            skPoint(sketch, "E392.newPointB", {"position": v(-215.1, 12.77) * mm});
            skArc(sketch, "E392.filletArc", {"start": v(-209.4, 13.51) * mm, "mid": v(-213.54, 11.64) * mm, "end": v(-215.37, 7.49) * mm});
            skPoint(sketch, "E393.newPointA", {"position": v(-215.48, -4.49) * mm});
            skPoint(sketch, "E393.newPointB", {"position": v(-215.94, -4) * mm});
            skArc(sketch, "E393.filletArc", {"start": v(-215.63, 2.19) * mm, "mid": v(-213.89, -2.5) * mm, "end": v(-209.28, -4.48) * mm});
            skPoint(sketch, "E394.visualSharp", {"position": v(73.75, 141.63) * mm});
            skArc(sketch, "E394.filletArc", {"start": v(75.35, 134.11) * mm, "mid": v(75.82, 138.14) * mm, "end": v(73.75, 141.63) * mm});
            skPoint(sketch, "E395.visualSharp", {"position": v(71.75, 143.36) * mm});
            skArc(sketch, "E395.filletArc", {"start": v(71.75, 143.36) * mm, "mid": v(68.27, 144.86) * mm, "end": v(64.56, 144.12) * mm});
            skSolve(sketch);
        }
        {
            var Q0;
            Q0=makeQuery(id+"F0.imprint","IMPRINT",FACE,{"disambiguationData":[TD([[makeQuery(id+"F0.imprint","IMPRINT",EDGE,{"derivedFrom":sQuery(id+"F0.wireOp",EDGE,"E103.bottom")}),-1.0]])]});
            var Q1;
            Q1=makeQuery(id+"F0.imprint","IMPRINT",FACE,{"disambiguationData":[TD([[makeQuery(id+"F0.imprint","IMPRINT",EDGE,{"derivedFrom":sQuery(id+"F0.wireOp",EDGE,"E109.bottom")}),-1.0]])]});
            var Q2;
            Q2=makeQuery(id+"F0.imprint","IMPRINT",FACE,{"disambiguationData":[TD([[makeQuery(id+"F0.imprint","IMPRINT",EDGE,{"derivedFrom":sQuery(id+"F0.wireOp",EDGE,"E112.bottom")}),-1.0]])]});
            var Q3;
            Q3=makeQuery(id+"F0.imprint","IMPRINT",FACE,{"disambiguationData":[TD([[makeQuery(id+"F0.imprint","IMPRINT",EDGE,{"derivedFrom":sQuery(id+"F0.wireOp",EDGE,"E115.bottom")}),-1.0]])]});
            var Q4;
            {var subQ0=sQuery(id+"F0.wireOp",EDGE,"E124.bottom");Q4=makeQuery(id+"F0.imprint","IMPRINT",FACE,{"disambiguationData":[TD([[makeQuery(id+"F0.imprint","IMPRINT",EDGE,{"derivedFrom":subQ0}),-1.0]])]});}
            var Q5;
            Q5=makeQuery(id+"F0.imprint","IMPRINT",FACE,{"disambiguationData":[TD([[makeQuery(id+"F0.imprint","IMPRINT",EDGE,{"derivedFrom":sQuery(id+"F0.wireOp",EDGE,"E118.bottom")}),-1.0]])]});
            var Q6;
            Q6=makeQuery(id+"F0.imprint","IMPRINT",FACE,{"disambiguationData":[TD([[makeQuery(id+"F0.imprint","IMPRINT",EDGE,{"derivedFrom":sQuery(id+"F0.wireOp",EDGE,"E121.bottom")}),-1.0]])]});
            var Q7;
            {var subQ0=sQuery(id+"F0.wireOp",EDGE,"E127.bottom");Q7=makeQuery(id+"F0.imprint","IMPRINT",FACE,{"disambiguationData":[TD([[makeQuery(id+"F0.imprint","IMPRINT",EDGE,{"derivedFrom":subQ0}),-1.0]])]});}
            var Q8;
            {var subQ0=sQuery(id+"F0.wireOp",EDGE,"E145.bottom");Q8=makeQuery(id+"F0.imprint","IMPRINT",FACE,{"disambiguationData":[TD([[makeQuery(id+"F0.imprint","IMPRINT",EDGE,{"derivedFrom":subQ0}),-1.0]])]});}
            var Q9;
            Q9=makeQuery(id+"F0.imprint","IMPRINT",FACE,{"disambiguationData":[TD([[makeQuery(id+"F0.imprint","IMPRINT",EDGE,{"derivedFrom":sQuery(id+"F0.wireOp",EDGE,"E136.bottom")}),-1.0]])]});
            var Q10;
            Q10=makeQuery(id+"F0.imprint","IMPRINT",FACE,{"disambiguationData":[TD([[makeQuery(id+"F0.imprint","IMPRINT",EDGE,{"derivedFrom":sQuery(id+"F0.wireOp",EDGE,"E158.MirrorCS")}),1.0]])]});
            var Q11;
            {var subQ0=sQuery(id+"F0.wireOp",EDGE,"E133.bottom");Q11=makeQuery(id+"F0.imprint","IMPRINT",FACE,{"disambiguationData":[TD([[makeQuery(id+"F0.imprint","IMPRINT",EDGE,{"derivedFrom":subQ0}),-1.0]])]});}
            var Q12;
            {var subQ0=sQuery(id+"F0.wireOp",EDGE,"E139.bottom");Q12=makeQuery(id+"F0.imprint","IMPRINT",FACE,{"disambiguationData":[TD([[makeQuery(id+"F0.imprint","IMPRINT",EDGE,{"derivedFrom":subQ0}),-1.0]])]});}
            var Q13;
            {var subQ0=sQuery(id+"F0.wireOp",EDGE,"E142.bottom");Q13=makeQuery(id+"F0.imprint","IMPRINT",FACE,{"disambiguationData":[TD([[makeQuery(id+"F0.imprint","IMPRINT",EDGE,{"derivedFrom":subQ0}),-1.0]])]});}
            var Q14;
            {var subQ0=sQuery(id+"F0.wireOp",EDGE,"E162.MirrorCS");Q14=makeQuery(id+"F0.imprint","IMPRINT",FACE,{"disambiguationData":[TD([[makeQuery(id+"F0.imprint","IMPRINT",EDGE,{"derivedFrom":subQ0}),1.0]])]});}
            var Q15;
            Q15=makeQuery(id+"F0.imprint","IMPRINT",FACE,{"disambiguationData":[TD([[makeQuery(id+"F0.imprint","IMPRINT",EDGE,{"derivedFrom":sQuery(id+"F0.wireOp",EDGE,"E173.MirrorCS")}),1.0]])]});
            var Q16;
            {var subQ0=sQuery(id+"F0.wireOp",EDGE,"E130.bottom");Q16=makeQuery(id+"F0.imprint","IMPRINT",FACE,{"disambiguationData":[TD([[makeQuery(id+"F0.imprint","IMPRINT",EDGE,{"derivedFrom":subQ0}),-1.0]])]});}
            var Q17;
            {var subQ0=sQuery(id+"F0.wireOp",EDGE,"E148.bottom");Q17=makeQuery(id+"F0.imprint","IMPRINT",FACE,{"disambiguationData":[TD([[makeQuery(id+"F0.imprint","IMPRINT",EDGE,{"derivedFrom":subQ0}),-1.0]])]});}
            var Q18;
            Q18=makeQuery(id+"F0.imprint","IMPRINT",FACE,{"disambiguationData":[TD([[makeQuery(id+"F0.imprint","IMPRINT",EDGE,{"derivedFrom":sQuery(id+"F0.wireOp",EDGE,"E106.bottom")}),-1.0]])]});
            var Q19;
            {var subQ1=sQuery(id+"F0.wireOp",EDGE,"E100.left");Q19=makeQuery(id+"F0.imprint","IMPRINT",FACE,{"disambiguationData":[TD([[makeQuery(id+"F0.imprint","IMPRINT",EDGE,{"derivedFrom":subQ1}),1.0]])]});}
            var Q20;
            {var subQ0=sQuery(id+"F0.wireOp",EDGE,"E118.top");Q20=makeQuery(id+"F0.imprint","IMPRINT",FACE,{"disambiguationData":[TD([[makeQuery(id+"F0.imprint","IMPRINT",EDGE,{"derivedFrom":subQ0}),1.0]])]});}
            var Q21;
            {var subQ0=sQuery(id+"F0.wireOp",EDGE,"E201.MirrorCS");Q21=makeQuery(id+"F0.imprint","IMPRINT",FACE,{"disambiguationData":[TD([[makeQuery(id+"F0.imprint","IMPRINT",EDGE,{"derivedFrom":subQ0}),-1.0]])]});}
            var Q22;
            {var subQ0=sQuery(id+"F0.wireOp",EDGE,"E204.MirrorCS");Q22=makeQuery(id+"F0.imprint","IMPRINT",FACE,{"disambiguationData":[TD([[makeQuery(id+"F0.imprint","IMPRINT",EDGE,{"derivedFrom":subQ0}),-1.0]])]});}
            var Q23;
            {var subQ0=sQuery(id+"F0.wireOp",EDGE,"E112.top");Q23=makeQuery(id+"F0.imprint","IMPRINT",FACE,{"disambiguationData":[TD([[makeQuery(id+"F0.imprint","IMPRINT",EDGE,{"derivedFrom":subQ0}),1.0]])]});}
            var Q24;
            {var subQ0=sQuery(id+"F0.wireOp",EDGE,"E207.MirrorCS");Q24=makeQuery(id+"F0.imprint","IMPRINT",FACE,{"disambiguationData":[TD([[makeQuery(id+"F0.imprint","IMPRINT",EDGE,{"derivedFrom":subQ0}),-1.0]])]});}
            var Q25;
            {var subQ0=sQuery(id+"F0.wireOp",EDGE,"E210.MirrorCS");Q25=makeQuery(id+"F0.imprint","IMPRINT",FACE,{"disambiguationData":[TD([[makeQuery(id+"F0.imprint","IMPRINT",EDGE,{"derivedFrom":subQ0}),-1.0]])]});}
            var Q26;
            {var subQ0=sQuery(id+"F0.wireOp",EDGE,"E202.MirrorCS");Q26=makeQuery(id+"F0.imprint","IMPRINT",FACE,{"disambiguationData":[TD([[makeQuery(id+"F0.imprint","IMPRINT",EDGE,{"derivedFrom":subQ0}),-1.0]])]});}
            var Q27;
            {var subQ0=sQuery(id+"F0.wireOp",EDGE,"E124.top");Q27=makeQuery(id+"F0.imprint","IMPRINT",FACE,{"disambiguationData":[TD([[makeQuery(id+"F0.imprint","IMPRINT",EDGE,{"derivedFrom":subQ0}),1.0]])]});}
            var Q28;
            {var subQ0=sQuery(id+"F0.wireOp",EDGE,"E208.MirrorCS");Q28=makeQuery(id+"F0.imprint","IMPRINT",FACE,{"disambiguationData":[TD([[makeQuery(id+"F0.imprint","IMPRINT",EDGE,{"derivedFrom":subQ0}),-1.0]])]});}
            var Q29;
            {var subQ0=sQuery(id+"F0.wireOp",EDGE,"E206.MirrorCS");Q29=makeQuery(id+"F0.imprint","IMPRINT",FACE,{"disambiguationData":[TD([[makeQuery(id+"F0.imprint","IMPRINT",EDGE,{"derivedFrom":subQ0}),-1.0]])]});}
            var Q30;
            {var subQ0=sQuery(id+"F0.wireOp",EDGE,"E245.MirrorCS");Q30=makeQuery(id+"F0.imprint","IMPRINT",FACE,{"disambiguationData":[TD([[makeQuery(id+"F0.imprint","IMPRINT",EDGE,{"derivedFrom":subQ0}),-1.0]])]});}
            var Q31;
            {var subQ0=sQuery(id+"F0.wireOp",EDGE,"E109.top");Q31=makeQuery(id+"F0.imprint","IMPRINT",FACE,{"disambiguationData":[TD([[makeQuery(id+"F0.imprint","IMPRINT",EDGE,{"derivedFrom":subQ0}),1.0]])]});}
            var Q32;
            {var subQ0=sQuery(id+"F0.wireOp",EDGE,"E130.top");Q32=makeQuery(id+"F0.imprint","IMPRINT",FACE,{"disambiguationData":[TD([[makeQuery(id+"F0.imprint","IMPRINT",EDGE,{"derivedFrom":subQ0}),1.0]])]});}
            var Q33;
            {var subQ0=sQuery(id+"F0.wireOp",EDGE,"E115.top");Q33=makeQuery(id+"F0.imprint","IMPRINT",FACE,{"disambiguationData":[TD([[makeQuery(id+"F0.imprint","IMPRINT",EDGE,{"derivedFrom":subQ0}),1.0]])]});}
            var Q34;
            {var subQ0=sQuery(id+"F0.wireOp",EDGE,"E145.top");Q34=makeQuery(id+"F0.imprint","IMPRINT",FACE,{"disambiguationData":[TD([[makeQuery(id+"F0.imprint","IMPRINT",EDGE,{"derivedFrom":subQ0}),1.0]])]});}
            var Q35;
            {var subQ0=sQuery(id+"F0.wireOp",EDGE,"E209.MirrorCS");Q35=makeQuery(id+"F0.imprint","IMPRINT",FACE,{"disambiguationData":[TD([[makeQuery(id+"F0.imprint","IMPRINT",EDGE,{"derivedFrom":subQ0}),-1.0]])]});}
            var Q36;
            {var subQ0=sQuery(id+"F0.wireOp",EDGE,"E133.top");Q36=makeQuery(id+"F0.imprint","IMPRINT",FACE,{"disambiguationData":[TD([[makeQuery(id+"F0.imprint","IMPRINT",EDGE,{"derivedFrom":subQ0}),1.0]])]});}
            var Q37;
            {var subQ0=sQuery(id+"F0.wireOp",EDGE,"E139.top");Q37=makeQuery(id+"F0.imprint","IMPRINT",FACE,{"disambiguationData":[TD([[makeQuery(id+"F0.imprint","IMPRINT",EDGE,{"derivedFrom":subQ0}),1.0]])]});}
            var Q38;
            {var subQ0=sQuery(id+"F0.wireOp",EDGE,"E103.top");Q38=makeQuery(id+"F0.imprint","IMPRINT",FACE,{"disambiguationData":[TD([[makeQuery(id+"F0.imprint","IMPRINT",EDGE,{"derivedFrom":subQ0}),1.0]])]});}
            var Q39;
            {var subQ0=sQuery(id+"F0.wireOp",EDGE,"E148.top");Q39=makeQuery(id+"F0.imprint","IMPRINT",FACE,{"disambiguationData":[TD([[makeQuery(id+"F0.imprint","IMPRINT",EDGE,{"derivedFrom":subQ0}),1.0]])]});}
            var Q40;
            {var subQ0=sQuery(id+"F0.wireOp",EDGE,"E274.MirrorCS");Q40=makeQuery(id+"F0.imprint","IMPRINT",FACE,{"disambiguationData":[TD([[makeQuery(id+"F0.imprint","IMPRINT",EDGE,{"derivedFrom":subQ0}),-1.0]])]});}
            var Q41;
            {var subQ0=sQuery(id+"F0.wireOp",EDGE,"E280.MirrorCS");Q41=makeQuery(id+"F0.imprint","IMPRINT",FACE,{"disambiguationData":[TD([[makeQuery(id+"F0.imprint","IMPRINT",EDGE,{"derivedFrom":subQ0}),-1.0]])]});}
            var Q42;
            {var subQ0=sQuery(id+"F0.wireOp",EDGE,"E100.top");Q42=makeQuery(id+"F0.imprint","IMPRINT",FACE,{"disambiguationData":[TD([[makeQuery(id+"F0.imprint","IMPRINT",EDGE,{"derivedFrom":subQ0}),1.0]])]});}
            var Q43;
            {var subQ0=sQuery(id+"F0.wireOp",EDGE,"E203.MirrorCS");Q43=makeQuery(id+"F0.imprint","IMPRINT",FACE,{"disambiguationData":[TD([[makeQuery(id+"F0.imprint","IMPRINT",EDGE,{"derivedFrom":subQ0}),-1.0]])]});}
            var Q44;
            {var subQ0=sQuery(id+"F0.wireOp",EDGE,"E211.MirrorCS");Q44=makeQuery(id+"F0.imprint","IMPRINT",FACE,{"disambiguationData":[TD([[makeQuery(id+"F0.imprint","IMPRINT",EDGE,{"derivedFrom":subQ0}),-1.0]])]});}
            var Q45;
            {var subQ0=sQuery(id+"F0.wireOp",EDGE,"E106.top");Q45=makeQuery(id+"F0.imprint","IMPRINT",FACE,{"disambiguationData":[TD([[makeQuery(id+"F0.imprint","IMPRINT",EDGE,{"derivedFrom":subQ0}),1.0]])]});}
            var Q46;
            {var subQ0=sQuery(id+"F0.wireOp",EDGE,"E142.top");Q46=makeQuery(id+"F0.imprint","IMPRINT",FACE,{"disambiguationData":[TD([[makeQuery(id+"F0.imprint","IMPRINT",EDGE,{"derivedFrom":subQ0}),1.0]])]});}
            var Q47;
            {var subQ0=sQuery(id+"F0.wireOp",EDGE,"E136.top");Q47=makeQuery(id+"F0.imprint","IMPRINT",FACE,{"disambiguationData":[TD([[makeQuery(id+"F0.imprint","IMPRINT",EDGE,{"derivedFrom":subQ0}),1.0]])]});}
            var Q48;
            {var subQ0=sQuery(id+"F0.wireOp",EDGE,"E205.MirrorCS");Q48=makeQuery(id+"F0.imprint","IMPRINT",FACE,{"disambiguationData":[TD([[makeQuery(id+"F0.imprint","IMPRINT",EDGE,{"derivedFrom":subQ0}),-1.0]])]});}
            var Q49;
            {var subQ0=sQuery(id+"F0.wireOp",EDGE,"E127.top");Q49=makeQuery(id+"F0.imprint","IMPRINT",FACE,{"disambiguationData":[TD([[makeQuery(id+"F0.imprint","IMPRINT",EDGE,{"derivedFrom":subQ0}),1.0]])]});}
            var Q50;
            {var subQ0=sQuery(id+"F0.wireOp",EDGE,"E232.MirrorCS");Q50=makeQuery(id+"F0.imprint","IMPRINT",FACE,{"disambiguationData":[TD([[makeQuery(id+"F0.imprint","IMPRINT",EDGE,{"derivedFrom":subQ0}),-1.0]])]});}
            var Q51;
            {var subQ0=sQuery(id+"F0.wireOp",EDGE,"E121.top");Q51=makeQuery(id+"F0.imprint","IMPRINT",FACE,{"disambiguationData":[TD([[makeQuery(id+"F0.imprint","IMPRINT",EDGE,{"derivedFrom":subQ0}),1.0]])]});}
            var Q52;
            {var subQ0=sQuery(id+"F0.wireOp",EDGE,"E212.MirrorCS");Q52=makeQuery(id+"F0.imprint","IMPRINT",FACE,{"disambiguationData":[TD([[makeQuery(id+"F0.imprint","IMPRINT",EDGE,{"derivedFrom":subQ0}),-1.0]])]});}
            var Q53;
            {var subQ1=sQuery(id+"F0.wireOp",EDGE,"E248.MirrorCS");Q53=makeQuery(id+"F0.imprint","IMPRINT",FACE,{"disambiguationData":[TD([[makeQuery(id+"F0.imprint","IMPRINT",EDGE,{"derivedFrom":subQ1}),1.0]])]});}
            var Q54;
            {var subQ1=sQuery(id+"F0.wireOp",EDGE,"E124.left");Q54=makeQuery(id+"F0.imprint","IMPRINT",FACE,{"disambiguationData":[TD([[makeQuery(id+"F0.imprint","IMPRINT",EDGE,{"derivedFrom":subQ1}),1.0]])]});}
            var Q55;
            {var subQ0=sQuery(id+"F0.wireOp",EDGE,"E238.MirrorCS");Q55=makeQuery(id+"F0.imprint","IMPRINT",FACE,{"disambiguationData":[TD([[makeQuery(id+"F0.imprint","IMPRINT",EDGE,{"derivedFrom":subQ0}),1.0]])]});}
            var Q56;
            {var subQ1=sQuery(id+"F0.wireOp",EDGE,"E130.left");Q56=makeQuery(id+"F0.imprint","IMPRINT",FACE,{"disambiguationData":[TD([[makeQuery(id+"F0.imprint","IMPRINT",EDGE,{"derivedFrom":subQ1}),1.0]])]});}
            var Q57;
            {var subQ2=sQuery(id+"F0.wireOp",EDGE,"E216.MirrorCS");Q57=makeQuery(id+"F0.imprint","IMPRINT",FACE,{"disambiguationData":[TD([[makeQuery(id+"F0.imprint","IMPRINT",EDGE,{"derivedFrom":subQ2}),1.0]])]});}
            var Q58;
            {var subQ1=sQuery(id+"F0.wireOp",EDGE,"E145.left");Q58=makeQuery(id+"F0.imprint","IMPRINT",FACE,{"disambiguationData":[TD([[makeQuery(id+"F0.imprint","IMPRINT",EDGE,{"derivedFrom":subQ1}),1.0]])]});}
            var Q59;
            {var subQ0=sQuery(id+"F0.wireOp",EDGE,"E148.left");Q59=makeQuery(id+"F0.imprint","IMPRINT",FACE,{"disambiguationData":[TD([[makeQuery(id+"F0.imprint","IMPRINT",EDGE,{"derivedFrom":subQ0}),1.0]])]});}
            var Q60;
            {var subQ1=sQuery(id+"F0.wireOp",EDGE,"E127.left");Q60=makeQuery(id+"F0.imprint","IMPRINT",FACE,{"disambiguationData":[TD([[makeQuery(id+"F0.imprint","IMPRINT",EDGE,{"derivedFrom":subQ1}),1.0]])]});}
            var Q61;
            {var subQ4=sQuery(id+"F0.wireOp",EDGE,"E217.MirrorCS");Q61=makeQuery(id+"F0.imprint","IMPRINT",FACE,{"disambiguationData":[TD([[makeQuery(id+"F0.imprint","IMPRINT",EDGE,{"derivedFrom":subQ4}),-1.0]])]});}
            var Q62;
            {var subQ0=sQuery(id+"F0.wireOp",EDGE,"E236.MirrorCS");Q62=makeQuery(id+"F0.imprint","IMPRINT",FACE,{"disambiguationData":[TD([[makeQuery(id+"F0.imprint","IMPRINT",EDGE,{"derivedFrom":subQ0}),-1.0]])]});}
            var Q63;
            {var subQ4=sQuery(id+"F0.wireOp",EDGE,"E259.MirrorCS");Q63=makeQuery(id+"F0.imprint","IMPRINT",FACE,{"disambiguationData":[TD([[makeQuery(id+"F0.imprint","IMPRINT",EDGE,{"derivedFrom":subQ4}),-1.0]])]});}
            var Q64;
            Q64=makeQuery(id+"F0.imprint","IMPRINT",FACE,{"disambiguationData":[TD([[makeQuery(id+"F0.imprint","IMPRINT",EDGE,{"derivedFrom":sQuery(id+"F0.wireOp",EDGE,"E194.MirrorCS")}),1.0]])]});
            var Q65;
            {var subQ1=sQuery(id+"F0.wireOp",EDGE,"E133.left");Q65=makeQuery(id+"F0.imprint","IMPRINT",FACE,{"disambiguationData":[TD([[makeQuery(id+"F0.imprint","IMPRINT",EDGE,{"derivedFrom":subQ1}),1.0]])]});}
            var Q66;
            {var subQ1=sQuery(id+"F0.wireOp",EDGE,"E142.left");Q66=makeQuery(id+"F0.imprint","IMPRINT",FACE,{"disambiguationData":[TD([[makeQuery(id+"F0.imprint","IMPRINT",EDGE,{"derivedFrom":subQ1}),1.0]])]});}
            var Q67;
            Q67=makeQuery(id+"F0.imprint","IMPRINT",FACE,{"disambiguationData":[TD([[makeQuery(id+"F0.imprint","IMPRINT",EDGE,{"derivedFrom":sQuery(id+"F0.wireOp",EDGE,"E178.MirrorCS")}),1.0]])]});
            var Q68;
            Q68=makeQuery(id+"F0.imprint","IMPRINT",FACE,{"disambiguationData":[TD([[makeQuery(id+"F0.imprint","IMPRINT",EDGE,{"derivedFrom":sQuery(id+"F0.wireOp",EDGE,"E185.MirrorCS")}),1.0]])]});
            var Q69;
            Q69=makeQuery(id+"F0.imprint","IMPRINT",FACE,{"disambiguationData":[TD([[makeQuery(id+"F0.imprint","IMPRINT",EDGE,{"derivedFrom":sQuery(id+"F0.wireOp",EDGE,"E161.MirrorCS")}),1.0]])]});
            var Q70;
            {var subQ1=sQuery(id+"F0.wireOp",EDGE,"E139.left");Q70=makeQuery(id+"F0.imprint","IMPRINT",FACE,{"disambiguationData":[TD([[makeQuery(id+"F0.imprint","IMPRINT",EDGE,{"derivedFrom":subQ1}),1.0]])]});}
            var Q71;
            Q71=makeQuery(id+"F0.imprint","IMPRINT",FACE,{"disambiguationData":[TD([[makeQuery(id+"F0.imprint","IMPRINT",EDGE,{"derivedFrom":sQuery(id+"F0.wireOp",EDGE,"E191.MirrorCS")}),1.0]])]});
            var Q72;
            Q72=makeQuery(id+"F0.imprint","IMPRINT",FACE,{"disambiguationData":[TD([[makeQuery(id+"F0.imprint","IMPRINT",EDGE,{"derivedFrom":sQuery(id+"F0.wireOp",EDGE,"E196.MirrorCS")}),1.0]])]});
            var Q73;
            {var subQ1=sQuery(id+"F0.wireOp",EDGE,"E233.MirrorCS");Q73=makeQuery(id+"F0.imprint","IMPRINT",FACE,{"disambiguationData":[TD([[makeQuery(id+"F0.imprint","IMPRINT",EDGE,{"derivedFrom":subQ1}),1.0]])]});}
            var Q74;
            {var subQ1=sQuery(id+"F0.wireOp",EDGE,"E218.MirrorCS");Q74=makeQuery(id+"F0.imprint","IMPRINT",FACE,{"disambiguationData":[TD([[makeQuery(id+"F0.imprint","IMPRINT",EDGE,{"derivedFrom":subQ1}),1.0]])]});}
            var Q75;
            {var subQ0=sQuery(id+"F0.wireOp",EDGE,"E183.MirrorCS");Q75=makeQuery(id+"F0.imprint","IMPRINT",FACE,{"disambiguationData":[TD([[makeQuery(id+"F0.imprint","IMPRINT",EDGE,{"derivedFrom":subQ0}),1.0]])]});}
            var Q76;
            {var subQ0=sQuery(id+"F0.wireOp",EDGE,"E157.MirrorCS");Q76=makeQuery(id+"F0.imprint","IMPRINT",FACE,{"disambiguationData":[TD([[makeQuery(id+"F0.imprint","IMPRINT",EDGE,{"derivedFrom":subQ0}),1.0]])]});}
            var Q77;
            {var subQ0=sQuery(id+"F0.wireOp",EDGE,"E188.MirrorCS");Q77=makeQuery(id+"F0.imprint","IMPRINT",FACE,{"disambiguationData":[TD([[makeQuery(id+"F0.imprint","IMPRINT",EDGE,{"derivedFrom":subQ0}),1.0]])]});}
            var Q78;
            {var subQ0=sQuery(id+"F0.wireOp",EDGE,"E174.MirrorCS");Q78=makeQuery(id+"F0.imprint","IMPRINT",FACE,{"disambiguationData":[TD([[makeQuery(id+"F0.imprint","IMPRINT",EDGE,{"derivedFrom":subQ0}),1.0]])]});}
            var Q79;
            {var subQ0=sQuery(id+"F0.wireOp",EDGE,"E175.MirrorCS");Q79=makeQuery(id+"F0.imprint","IMPRINT",FACE,{"disambiguationData":[TD([[makeQuery(id+"F0.imprint","IMPRINT",EDGE,{"derivedFrom":subQ0}),1.0]])]});}
            var Q80;
            {var subQ0=sQuery(id+"F0.wireOp",EDGE,"E200.MirrorCS");Q80=makeQuery(id+"F0.imprint","IMPRINT",FACE,{"disambiguationData":[TD([[makeQuery(id+"F0.imprint","IMPRINT",EDGE,{"derivedFrom":subQ0}),1.0]])]});}
            var Q81;
            {var subQ0=sQuery(id+"F0.wireOp",EDGE,"E199.MirrorCS");Q81=makeQuery(id+"F0.imprint","IMPRINT",FACE,{"disambiguationData":[TD([[makeQuery(id+"F0.imprint","IMPRINT",EDGE,{"derivedFrom":subQ0}),1.0]])]});}
            var Q82;
            {var subQ2=sQuery(id+"F0.wireOp",EDGE,"E100.top");Q82=makeQuery(id+"F0.imprint","IMPRINT",FACE,{"disambiguationData":[TD([[makeQuery(id+"F0.imprint","IMPRINT",EDGE,{"derivedFrom":subQ2}),-1.0]])]});}
            extrude(context, id + "F1", {"entities" : qUnion([Q0, Q1, Q2, Q3, Q4, Q5, Q6, Q7, Q8, Q9, Q10, Q11, Q12, Q13, Q14, Q15, Q16, Q17, Q18, Q19, Q20, Q21, Q22, Q23, Q24, Q25, Q26, Q27, Q28, Q29, Q30, Q31, Q32, Q33, Q34, Q35, Q36, Q37, Q38, Q39, Q40, Q41, Q42, Q43, Q44, Q45, Q46, Q47, Q48, Q49, Q50, Q51, Q52, Q53, Q54, Q55, Q56, Q57, Q58, Q59, Q60, Q61, Q62, Q63, Q64, Q65, Q66, Q67, Q68, Q69, Q70, Q71, Q72, Q73, Q74, Q75, Q76, Q77, Q78, Q79, Q80, Q81, Q82]), "depth" : 12.7 * mm});
        }
        {
            var Q0;
            Q0=makeQuery(id+"F0.imprint","IMPRINT",FACE,{"disambiguationData":[TD([[makeQuery(id+"F0.imprint","IMPRINT",EDGE,{"derivedFrom":sQuery(id+"F0.wireOp",EDGE,"E3")}),-1.0]])]});
            var Q1;
            Q1=makeQuery(id+"F0.imprint","IMPRINT",FACE,{"disambiguationData":[TD([[makeQuery(id+"F0.imprint","IMPRINT",EDGE,{"derivedFrom":sQuery(id+"F0.wireOp",EDGE,"E23.bottom")}),-1.0]])]});
            var Q2;
            Q2=makeQuery(id+"F0.imprint","IMPRINT",FACE,{"disambiguationData":[TD([[makeQuery(id+"F0.imprint","IMPRINT",EDGE,{"derivedFrom":sQuery(id+"F0.wireOp",EDGE,"E32.bottom")}),-1.0]])]});
            var Q3;
            Q3=makeQuery(id+"F0.imprint","IMPRINT",FACE,{"disambiguationData":[TD([[makeQuery(id+"F0.imprint","IMPRINT",EDGE,{"derivedFrom":sQuery(id+"F0.wireOp",EDGE,"E39.MirrorCS")}),1.0]])]});
            var Q4;
            Q4=makeQuery(id+"F0.imprint","IMPRINT",FACE,{"disambiguationData":[TD([[makeQuery(id+"F0.imprint","IMPRINT",EDGE,{"derivedFrom":sQuery(id+"F0.wireOp",EDGE,"E29.bottom")}),-1.0]])]});
            var Q5;
            Q5=makeQuery(id+"F0.imprint","IMPRINT",FACE,{"disambiguationData":[TD([[makeQuery(id+"F0.imprint","IMPRINT",EDGE,{"derivedFrom":sQuery(id+"F0.wireOp",EDGE,"E26.bottom")}),-1.0]])]});
            var Q6;
            Q6=makeQuery(id+"F0.imprint","IMPRINT",FACE,{"disambiguationData":[TD([[makeQuery(id+"F0.imprint","IMPRINT",EDGE,{"derivedFrom":sQuery(id+"F0.wireOp",EDGE,"E11.bottom")}),-1.0]])]});
            var Q7;
            Q7=makeQuery(id+"F0.imprint","IMPRINT",FACE,{"disambiguationData":[TD([[makeQuery(id+"F0.imprint","IMPRINT",EDGE,{"derivedFrom":sQuery(id+"F0.wireOp",EDGE,"E8.bottom")}),-1.0]])]});
            var Q8;
            Q8=makeQuery(id+"F0.imprint","IMPRINT",FACE,{"disambiguationData":[TD([[makeQuery(id+"F0.imprint","IMPRINT",EDGE,{"derivedFrom":sQuery(id+"F0.wireOp",EDGE,"E5.bottom")}),-1.0]])]});
            var Q9;
            Q9=makeQuery(id+"F0.imprint","IMPRINT",FACE,{"disambiguationData":[TD([[makeQuery(id+"F0.imprint","IMPRINT",EDGE,{"derivedFrom":sQuery(id+"F0.wireOp",EDGE,"E14.bottom")}),-1.0]])]});
            var Q10;
            Q10=makeQuery(id+"F0.imprint","IMPRINT",FACE,{"disambiguationData":[TD([[makeQuery(id+"F0.imprint","IMPRINT",EDGE,{"derivedFrom":sQuery(id+"F0.wireOp",EDGE,"E17.bottom")}),-1.0]])]});
            var Q11;
            Q11=makeQuery(id+"F0.imprint","IMPRINT",FACE,{"disambiguationData":[TD([[makeQuery(id+"F0.imprint","IMPRINT",EDGE,{"derivedFrom":sQuery(id+"F0.wireOp",EDGE,"E20.bottom")}),-1.0]])]});
            var Q12;
            {var subQ0=sQuery(id+"F0.wireOp",EDGE,"E98.MirrorCS");Q12=makeQuery(id+"F0.imprint","IMPRINT",FACE,{"disambiguationData":[TD([[makeQuery(id+"F0.imprint","IMPRINT",EDGE,{"derivedFrom":subQ0}),-1.0]])]});}
            var Q13;
            {var subQ0=sQuery(id+"F0.wireOp",EDGE,"E26.top");Q13=makeQuery(id+"F0.imprint","IMPRINT",FACE,{"disambiguationData":[TD([[makeQuery(id+"F0.imprint","IMPRINT",EDGE,{"derivedFrom":subQ0}),1.0]])]});}
            var Q14;
            {var subQ0=sQuery(id+"F0.wireOp",EDGE,"E11.top");Q14=makeQuery(id+"F0.imprint","IMPRINT",FACE,{"disambiguationData":[TD([[makeQuery(id+"F0.imprint","IMPRINT",EDGE,{"derivedFrom":subQ0}),1.0]])]});}
            var Q15;
            {var subQ0=sQuery(id+"F0.wireOp",EDGE,"E74.MirrorCS");Q15=makeQuery(id+"F0.imprint","IMPRINT",FACE,{"disambiguationData":[TD([[makeQuery(id+"F0.imprint","IMPRINT",EDGE,{"derivedFrom":subQ0}),-1.0]])]});}
            var Q16;
            {var subQ0=sQuery(id+"F0.wireOp",EDGE,"E8.top");Q16=makeQuery(id+"F0.imprint","IMPRINT",FACE,{"disambiguationData":[TD([[makeQuery(id+"F0.imprint","IMPRINT",EDGE,{"derivedFrom":subQ0}),1.0]])]});}
            var Q17;
            {var subQ0=sQuery(id+"F0.wireOp",EDGE,"E17.top");Q17=makeQuery(id+"F0.imprint","IMPRINT",FACE,{"disambiguationData":[TD([[makeQuery(id+"F0.imprint","IMPRINT",EDGE,{"derivedFrom":subQ0}),1.0]])]});}
            var Q18;
            {var subQ0=sQuery(id+"F0.wireOp",EDGE,"E5.top");Q18=makeQuery(id+"F0.imprint","IMPRINT",FACE,{"disambiguationData":[TD([[makeQuery(id+"F0.imprint","IMPRINT",EDGE,{"derivedFrom":subQ0}),1.0]])]});}
            var Q19;
            {var subQ0=sQuery(id+"F0.wireOp",EDGE,"E14.top");Q19=makeQuery(id+"F0.imprint","IMPRINT",FACE,{"disambiguationData":[TD([[makeQuery(id+"F0.imprint","IMPRINT",EDGE,{"derivedFrom":subQ0}),1.0]])]});}
            var Q20;
            {var subQ0=sQuery(id+"F0.wireOp",EDGE,"E20.top");Q20=makeQuery(id+"F0.imprint","IMPRINT",FACE,{"disambiguationData":[TD([[makeQuery(id+"F0.imprint","IMPRINT",EDGE,{"derivedFrom":subQ0}),1.0]])]});}
            var Q21;
            {var subQ0=sQuery(id+"F0.wireOp",EDGE,"E23.top");Q21=makeQuery(id+"F0.imprint","IMPRINT",FACE,{"disambiguationData":[TD([[makeQuery(id+"F0.imprint","IMPRINT",EDGE,{"derivedFrom":subQ0}),1.0]])]});}
            var Q22;
            {var subQ0=sQuery(id+"F0.wireOp",EDGE,"E84.MirrorCS");Q22=makeQuery(id+"F0.imprint","IMPRINT",FACE,{"disambiguationData":[TD([[makeQuery(id+"F0.imprint","IMPRINT",EDGE,{"derivedFrom":subQ0}),-1.0]])]});}
            var Q23;
            {var subQ0=sQuery(id+"F0.wireOp",EDGE,"E68.MirrorCS");Q23=makeQuery(id+"F0.imprint","IMPRINT",FACE,{"disambiguationData":[TD([[makeQuery(id+"F0.imprint","IMPRINT",EDGE,{"derivedFrom":subQ0}),-1.0]])]});}
            var Q24;
            {var subQ0=sQuery(id+"F0.wireOp",EDGE,"E97.MirrorCS");Q24=makeQuery(id+"F0.imprint","IMPRINT",FACE,{"disambiguationData":[TD([[makeQuery(id+"F0.imprint","IMPRINT",EDGE,{"derivedFrom":subQ0}),-1.0]])]});}
            var Q25;
            {var subQ0=sQuery(id+"F0.wireOp",EDGE,"E73.MirrorCS");Q25=makeQuery(id+"F0.imprint","IMPRINT",FACE,{"disambiguationData":[TD([[makeQuery(id+"F0.imprint","IMPRINT",EDGE,{"derivedFrom":subQ0}),-1.0]])]});}
            var Q26;
            {var subQ0=sQuery(id+"F0.wireOp",EDGE,"E88.MirrorCS");Q26=makeQuery(id+"F0.imprint","IMPRINT",FACE,{"disambiguationData":[TD([[makeQuery(id+"F0.imprint","IMPRINT",EDGE,{"derivedFrom":subQ0}),-1.0]])]});}
            var Q27;
            {var subQ0=sQuery(id+"F0.wireOp",EDGE,"E32.top");Q27=makeQuery(id+"F0.imprint","IMPRINT",FACE,{"disambiguationData":[TD([[makeQuery(id+"F0.imprint","IMPRINT",EDGE,{"derivedFrom":subQ0}),1.0]])]});}
            var Q28;
            {var subQ0=sQuery(id+"F0.wireOp",EDGE,"E92.MirrorCS");Q28=makeQuery(id+"F0.imprint","IMPRINT",FACE,{"disambiguationData":[TD([[makeQuery(id+"F0.imprint","IMPRINT",EDGE,{"derivedFrom":subQ0}),-1.0]])]});}
            var Q29;
            {var subQ0=sQuery(id+"F0.wireOp",EDGE,"E29.top");Q29=makeQuery(id+"F0.imprint","IMPRINT",FACE,{"disambiguationData":[TD([[makeQuery(id+"F0.imprint","IMPRINT",EDGE,{"derivedFrom":subQ0}),1.0]])]});}
            var Q30;
            Q30=makeQuery(id+"F0.imprint","IMPRINT",FACE,{"disambiguationData":[TD([[makeQuery(id+"F0.imprint","IMPRINT",EDGE,{"derivedFrom":sQuery(id+"F0.wireOp",EDGE,"E53.MirrorCS")}),1.0]])]});
            var Q31;
            Q31=makeQuery(id+"F0.imprint","IMPRINT",FACE,{"disambiguationData":[TD([[makeQuery(id+"F0.imprint","IMPRINT",EDGE,{"derivedFrom":sQuery(id+"F0.wireOp",EDGE,"E51.MirrorCS")}),1.0]])]});
            var Q32;
            Q32=makeQuery(id+"F0.imprint","IMPRINT",FACE,{"disambiguationData":[TD([[makeQuery(id+"F0.imprint","IMPRINT",EDGE,{"derivedFrom":sQuery(id+"F0.wireOp",EDGE,"E55.MirrorCS")}),1.0]])]});
            var Q33;
            Q33=makeQuery(id+"F0.imprint","IMPRINT",FACE,{"disambiguationData":[TD([[makeQuery(id+"F0.imprint","IMPRINT",EDGE,{"derivedFrom":sQuery(id+"F0.wireOp",EDGE,"E48.MirrorCS")}),1.0]])]});
            var Q34;
            Q34=makeQuery(id+"F0.imprint","IMPRINT",FACE,{"disambiguationData":[TD([[makeQuery(id+"F0.imprint","IMPRINT",EDGE,{"derivedFrom":sQuery(id+"F0.wireOp",EDGE,"E44.MirrorCS")}),1.0]])]});
            var Q35;
            Q35=makeQuery(id+"F0.imprint","IMPRINT",FACE,{"disambiguationData":[TD([[makeQuery(id+"F0.imprint","IMPRINT",EDGE,{"derivedFrom":sQuery(id+"F0.wireOp",EDGE,"E57.MirrorCS")}),1.0]])]});
            var Q36;
            Q36=makeQuery(id+"F0.imprint","IMPRINT",FACE,{"disambiguationData":[TD([[makeQuery(id+"F0.imprint","IMPRINT",EDGE,{"derivedFrom":sQuery(id+"F0.wireOp",EDGE,"E308.bottom")}),-1.0]])]});
            var Q37;
            Q37=makeQuery(id+"F0.imprint","IMPRINT",FACE,{"disambiguationData":[TD([[makeQuery(id+"F0.imprint","IMPRINT",EDGE,{"derivedFrom":sQuery(id+"F0.wireOp",EDGE,"E303.bottom")}),-1.0]])]});
            var Q38;
            Q38=makeQuery(id+"F0.imprint","IMPRINT",FACE,{"disambiguationData":[TD([[makeQuery(id+"F0.imprint","IMPRINT",EDGE,{"derivedFrom":sQuery(id+"F0.wireOp",EDGE,"E45.MirrorCS")}),1.0]])]});
            var Q39;
            {var subQ0=sQuery(id+"F0.wireOp",EDGE,"E303.top");Q39=makeQuery(id+"F0.imprint","IMPRINT",FACE,{"disambiguationData":[TD([[makeQuery(id+"F0.imprint","IMPRINT",EDGE,{"derivedFrom":subQ0}),1.0]])]});}
            var Q40;
            {var subQ0=sQuery(id+"F0.wireOp",EDGE,"E308.top");Q40=makeQuery(id+"F0.imprint","IMPRINT",FACE,{"disambiguationData":[TD([[makeQuery(id+"F0.imprint","IMPRINT",EDGE,{"derivedFrom":subQ0}),1.0]])]});}
            extrude(context, id + "F2", {"entities" : qUnion([Q0, Q1, Q2, Q3, Q4, Q5, Q6, Q7, Q8, Q9, Q10, Q11, Q12, Q13, Q14, Q15, Q16, Q17, Q18, Q19, Q20, Q21, Q22, Q23, Q24, Q25, Q26, Q27, Q28, Q29, Q30, Q31, Q32, Q33, Q34, Q35, Q36, Q37, Q38, Q39, Q40]), "depth" : 6.35 * mm});
        }
    });
